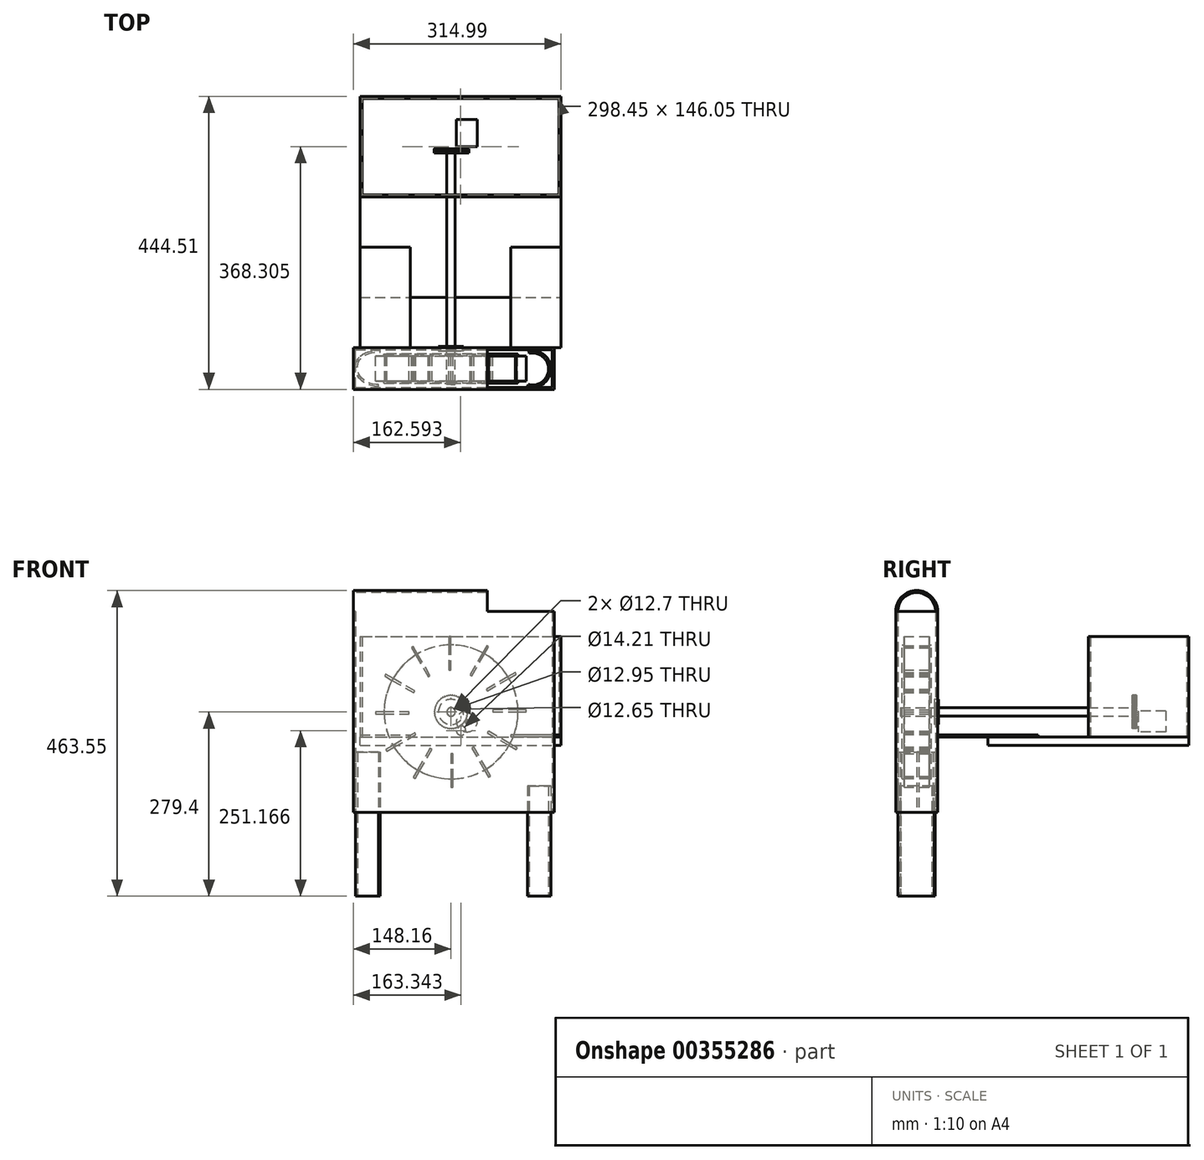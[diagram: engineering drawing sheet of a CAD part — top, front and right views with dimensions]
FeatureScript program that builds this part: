
annotation { "Feature Type Name" : "Feature", "Feature Type Description" : "" }
export const myFeature = defineFeature(function(context is Context, id is Id, definition is map)
    precondition{}
    {
        {
            var Q0;
            Q0=qCreatedBy(makeId("Front.planeOp"),FACE);
            var sketch = newSketch(context, id + "F0", { "sketchPlane" : qUnion([Q0])});
            skCircle(sketch, "E0", {"center": v(0, 0) * mm, "radius": 101.6 * mm});
            skCircle(sketch, "E1", {"center": v(0, 0) * mm, "radius": 6.35 * mm});
            skSolve(sketch);
        }
        {
            var Q0;
            Q0 = qSketchRegion(id + "F0", true);
            extrude(context, id + "F1", {"entities" : qUnion([Q0]), "depth" : 3.17 * mm});
        }
        {
            var Q0;
            Q0=makeQuery(id+"F1.opExtrude","CAP_FACE",FACE,{"disambiguationData":[OSD([sQuery(id+"F0.wireOp",EDGE,"E0"),sQuery(id+"F0.wireOp",EDGE,"E1")])],"isStart":false});
            var sketch = newSketch(context, id + "F2", { "sketchPlane" : qUnion([Q0])});
            skLineSegment(sketch, "E2", {"start": v(0, 101.6) * mm, "end": v(0, 63.5) * mm});
            skLineSegment(sketch, "E3", {"start": v(0, 101.6) * mm, "end": v(0, 114.3) * mm});
            skLineSegment(sketch, "E4", {"start": v(0, 114.3) * mm, "end": v(-3.18, 114.3) * mm});
            skLineSegment(sketch, "E5", {"start": v(-3.17, 114.3) * mm, "end": v(-3.17, 63.5) * mm});
            skLineSegment(sketch, "E6", {"start": v(-3.18, 63.5) * mm, "end": v(0, 63.5) * mm});
            skLineSegment(sketch, "E7.1.0", {"start": v(-59.9, 97.4) * mm, "end": v(-34.5, 53.4) * mm});
            skLineSegment(sketch, "E7.1.1", {"start": v(-50.8, 87.99) * mm, "end": v(-31.75, 55) * mm});
            skLineSegment(sketch, "E7.1.2", {"start": v(-34.5, 53.4) * mm, "end": v(-31.75, 55) * mm});
            skLineSegment(sketch, "E7.1.3", {"start": v(-50.8, 87.99) * mm, "end": v(-57.15, 98.99) * mm});
            skLineSegment(sketch, "E7.1.4", {"start": v(-57.15, 98.99) * mm, "end": v(-59.9, 97.4) * mm});
            skLineSegment(sketch, "E7.2.0", {"start": v(-100.57, 54.4) * mm, "end": v(-56.58, 29) * mm});
            skLineSegment(sketch, "E7.2.1", {"start": v(-87.99, 50.8) * mm, "end": v(-55, 31.75) * mm});
            skLineSegment(sketch, "E7.2.2", {"start": v(-56.58, 29) * mm, "end": v(-55, 31.75) * mm});
            skLineSegment(sketch, "E7.2.3", {"start": v(-87.99, 50.8) * mm, "end": v(-98.99, 57.15) * mm});
            skLineSegment(sketch, "E7.2.4", {"start": v(-98.99, 57.15) * mm, "end": v(-100.57, 54.4) * mm});
            skLineSegment(sketch, "E7.3.0", {"start": v(-114.3, -3.17) * mm, "end": v(-63.5, -3.17) * mm});
            skLineSegment(sketch, "E7.3.1", {"start": v(-101.6, 0) * mm, "end": v(-63.5, 0) * mm});
            skLineSegment(sketch, "E7.3.2", {"start": v(-63.5, -3.17) * mm, "end": v(-63.5, 0) * mm});
            skLineSegment(sketch, "E7.3.3", {"start": v(-101.6, 0) * mm, "end": v(-114.3, 0) * mm});
            skLineSegment(sketch, "E7.3.4", {"start": v(-114.3, 0) * mm, "end": v(-114.3, -3.17) * mm});
            skLineSegment(sketch, "E7.4.0", {"start": v(-97.4, -59.9) * mm, "end": v(-53.4, -34.5) * mm});
            skLineSegment(sketch, "E7.4.1", {"start": v(-87.99, -50.8) * mm, "end": v(-55, -31.75) * mm});
            skLineSegment(sketch, "E7.4.2", {"start": v(-53.4, -34.5) * mm, "end": v(-55, -31.75) * mm});
            skLineSegment(sketch, "E7.4.3", {"start": v(-87.99, -50.8) * mm, "end": v(-98.99, -57.15) * mm});
            skLineSegment(sketch, "E7.4.4", {"start": v(-98.99, -57.15) * mm, "end": v(-97.4, -59.9) * mm});
            skLineSegment(sketch, "E7.5.0", {"start": v(-54.4, -100.57) * mm, "end": v(-29, -56.58) * mm});
            skLineSegment(sketch, "E7.5.1", {"start": v(-50.8, -87.99) * mm, "end": v(-31.75, -55) * mm});
            skLineSegment(sketch, "E7.5.2", {"start": v(-29, -56.58) * mm, "end": v(-31.75, -55) * mm});
            skLineSegment(sketch, "E7.5.3", {"start": v(-50.8, -87.99) * mm, "end": v(-57.15, -98.99) * mm});
            skLineSegment(sketch, "E7.5.4", {"start": v(-57.15, -98.99) * mm, "end": v(-54.4, -100.57) * mm});
            skLineSegment(sketch, "E7.6.0", {"start": v(3.17, -114.3) * mm, "end": v(3.17, -63.5) * mm});
            skLineSegment(sketch, "E7.6.1", {"start": v(0, -101.6) * mm, "end": v(0, -63.5) * mm});
            skLineSegment(sketch, "E7.6.2", {"start": v(3.17, -63.5) * mm, "end": v(0, -63.5) * mm});
            skLineSegment(sketch, "E7.6.3", {"start": v(0, -101.6) * mm, "end": v(0, -114.3) * mm});
            skLineSegment(sketch, "E7.6.4", {"start": v(0, -114.3) * mm, "end": v(3.17, -114.3) * mm});
            skLineSegment(sketch, "E7.7.0", {"start": v(59.9, -97.4) * mm, "end": v(34.5, -53.4) * mm});
            skLineSegment(sketch, "E7.7.1", {"start": v(50.8, -87.99) * mm, "end": v(31.75, -55) * mm});
            skLineSegment(sketch, "E7.7.2", {"start": v(34.5, -53.4) * mm, "end": v(31.75, -55) * mm});
            skLineSegment(sketch, "E7.7.3", {"start": v(50.8, -87.99) * mm, "end": v(57.15, -98.99) * mm});
            skLineSegment(sketch, "E7.7.4", {"start": v(57.15, -98.99) * mm, "end": v(59.9, -97.4) * mm});
            skLineSegment(sketch, "E7.8.0", {"start": v(100.57, -54.4) * mm, "end": v(56.58, -29) * mm});
            skLineSegment(sketch, "E7.8.1", {"start": v(87.99, -50.8) * mm, "end": v(55, -31.75) * mm});
            skLineSegment(sketch, "E7.8.2", {"start": v(56.58, -29) * mm, "end": v(55, -31.75) * mm});
            skLineSegment(sketch, "E7.8.3", {"start": v(87.99, -50.8) * mm, "end": v(98.99, -57.15) * mm});
            skLineSegment(sketch, "E7.8.4", {"start": v(98.99, -57.15) * mm, "end": v(100.57, -54.4) * mm});
            skLineSegment(sketch, "E7.9.0", {"start": v(114.3, 3.17) * mm, "end": v(63.5, 3.17) * mm});
            skLineSegment(sketch, "E7.9.1", {"start": v(101.6, 0) * mm, "end": v(63.5, 0) * mm});
            skLineSegment(sketch, "E7.9.2", {"start": v(63.5, 3.17) * mm, "end": v(63.5, 0) * mm});
            skLineSegment(sketch, "E7.9.3", {"start": v(101.6, 0) * mm, "end": v(114.3, 0) * mm});
            skLineSegment(sketch, "E7.9.4", {"start": v(114.3, 0) * mm, "end": v(114.3, 3.17) * mm});
            skLineSegment(sketch, "E7.10.0", {"start": v(97.4, 59.9) * mm, "end": v(53.4, 34.5) * mm});
            skLineSegment(sketch, "E7.10.1", {"start": v(87.99, 50.8) * mm, "end": v(55, 31.75) * mm});
            skLineSegment(sketch, "E7.10.2", {"start": v(53.4, 34.5) * mm, "end": v(55, 31.75) * mm});
            skLineSegment(sketch, "E7.10.3", {"start": v(87.99, 50.8) * mm, "end": v(98.99, 57.15) * mm});
            skLineSegment(sketch, "E7.10.4", {"start": v(98.99, 57.15) * mm, "end": v(97.4, 59.9) * mm});
            skLineSegment(sketch, "E7.11.0", {"start": v(54.4, 100.57) * mm, "end": v(29, 56.58) * mm});
            skLineSegment(sketch, "E7.11.1", {"start": v(50.8, 87.99) * mm, "end": v(31.75, 55) * mm});
            skLineSegment(sketch, "E7.11.2", {"start": v(29, 56.58) * mm, "end": v(31.75, 55) * mm});
            skLineSegment(sketch, "E7.11.3", {"start": v(50.8, 87.99) * mm, "end": v(57.15, 98.99) * mm});
            skLineSegment(sketch, "E7.11.4", {"start": v(57.15, 98.99) * mm, "end": v(54.4, 100.57) * mm});
            skPoint(sketch, "E7.center", {"position": v(0, 0) * mm});
            skSolve(sketch);
        }
        {
            var Q0;
            Q0 = qSketchRegion(id + "F2", true);
            extrude(context, id + "F3", {"entities" : qUnion([Q0]), "operationType" : NewBodyOperationType.ADD, "depth" : 38.1 * mm});
        }
        {
            var Q0;
            Q0=makeQuery(id+"F3.opExtrude","CAP_FACE",FACE,{"disambiguationData":[OSD([sQuery(id+"F2.wireOp",EDGE,"E7.8.0"),sQuery(id+"F2.wireOp",EDGE,"E7.8.1"),sQuery(id+"F2.wireOp",EDGE,"E7.8.2"),sQuery(id+"F2.wireOp",EDGE,"E7.8.3"),sQuery(id+"F2.wireOp",EDGE,"E7.8.4")])],"isStart":false});
            var sketch = newSketch(context, id + "F4", { "sketchPlane" : qUnion([Q0])});
            skCircle(sketch, "E8", {"center": v(0, 0) * mm, "radius": 101.6 * mm});
            skCircle(sketch, "E9", {"center": v(0, 0) * mm, "radius": 6.35 * mm});
            skCircle(sketch, "E10", {"center": v(0, 0) * mm, "radius": 6.47 * mm});
            skSolve(sketch);
        }
        {
            var Q0;
            Q0 = qSketchRegion(id + "F4", true);
            extrude(context, id + "F5", {"entities" : qUnion([Q0]), "operationType" : NewBodyOperationType.ADD, "depth" : 3.17 * mm});
        }
        {
            var Q0;
            Q0=qCreatedBy(makeId("Front.planeOp"),FACE);
            var sketch = newSketch(context, id + "F6", { "sketchPlane" : qUnion([Q0])});
            skCircle(sketch, "E11", {"center": v(0, 0) * mm, "radius": 6.35 * mm});
            skSolve(sketch);
        }
        {
            var Q0;
            Q0 = qSketchRegion(id + "F6", true);
            extrude(context, id + "F7", {"entities" : qUnion([Q0]), "depth" : 46.74 * mm, "hasSecondDirection" : true, "secondDirectionOppositeDirection" : true, "secondDirectionDepth" : 304.8 * mm});
        }
        {
            var Q0;
            Q0=qCreatedBy(makeId("Top.planeOp"),FACE);
            var sketch = newSketch(context, id + "F8", { "sketchPlane" : qUnion([Q0])});
            skLineSegment(sketch, "E12.bottom", {"start": v(-148.16, 9.53) * mm, "end": v(156.64, 9.53) * mm});
            skLineSegment(sketch, "E12.top", {"start": v(-148.16, -53.97) * mm, "end": v(156.64, -53.97) * mm});
            skLineSegment(sketch, "E12.left", {"start": v(-148.16, 9.53) * mm, "end": v(-148.16, -53.97) * mm});
            skLineSegment(sketch, "E12.right", {"start": v(156.64, 9.52) * mm, "end": v(156.64, -53.97) * mm});
            skLineSegment(sketch, "E13.bottom", {"start": v(-144.98, -50.8) * mm, "end": v(153.47, -50.8) * mm});
            skLineSegment(sketch, "E13.top", {"start": v(-144.98, 6.35) * mm, "end": v(153.47, 6.35) * mm});
            skLineSegment(sketch, "E13.left", {"start": v(-144.98, -50.8) * mm, "end": v(-144.98, 6.35) * mm});
            skLineSegment(sketch, "E13.right", {"start": v(153.47, -50.8) * mm, "end": v(153.47, 6.35) * mm});
            skSolve(sketch);
        }
        {
            var Q0;
            Q0 = qSketchRegion(id + "F8", true);
            extrude(context, id + "F9", {"entities" : qUnion([Q0]), "depth" : 152.4 * mm, "hasSecondDirection" : true, "secondDirectionOppositeDirection" : true, "secondDirectionDepth" : 152.4 * mm});
        }
        {
            var Q0;
            Q0=makeQuery(id+"F9.opExtrude","SWEPT_FACE",FACE,{"disambiguationData":[OSD([sQuery(id+"F8.wireOp",EDGE,"E12.bottom")])]});
            var sketch = newSketch(context, id + "F10", { "sketchPlane" : qUnion([Q0])});
            skCircle(sketch, "E14", {"center": v(0, 0) * mm, "radius": 6.35 * mm});
            skCircle(sketch, "E15", {"center": v(0, 0) * mm, "radius": 19.05 * mm});
            skSolve(sketch);
        }
        {
            var Q0;
            Q0=makeQuery(id+"F10.imprint","IMPRINT",FACE,{"disambiguationData":[TD([[makeQuery(id+"F10.imprint","IMPRINT",EDGE,{"derivedFrom":sQuery(id+"F10.wireOp",EDGE,"E14")}),1.0]])]});
            extrude(context, id + "F11", {"entities" : qUnion([Q0]), "operationType" : NewBodyOperationType.REMOVE, "oppositeDirection" : true, "depth" : 3.17 * mm});
        }
        {
            var Q0;
            Q0=makeQuery(id+"F9.opExtrude","SWEPT_FACE",FACE,{"disambiguationData":[OSD([sQuery(id+"F8.wireOp",EDGE,"E12.bottom")])]});
            var sketch = newSketch(context, id + "F12", { "sketchPlane" : qUnion([Q0])});
            skCircle(sketch, "E16", {"center": v(0, 0) * mm, "radius": 19.05 * mm});
            skCircle(sketch, "E17", {"center": v(0, 0) * mm, "radius": 6.33 * mm});
            skSolve(sketch);
        }
        {
            var Q0;
            Q0 = qSketchRegion(id + "F12", true);
            extrude(context, id + "F13", {"entities" : qUnion([Q0]), "depth" : 1.63 * mm, "hasSecondDirection" : true, "secondDirectionOppositeDirection" : true, "secondDirectionDepth" : 5.23 * mm});
        }
        {
            var Q0;
            Q0=qCreatedBy(makeId("Top.planeOp"),FACE);
            var sketch = newSketch(context, id + "F14", { "sketchPlane" : qUnion([Q0])});
            skLineSegment(sketch, "E18.bottom", {"start": v(-137.97, 85.72) * mm, "end": v(166.83, 85.72) * mm});
            skLineSegment(sketch, "E18.top", {"start": v(-137.97, 390.53) * mm, "end": v(166.83, 390.53) * mm});
            skLineSegment(sketch, "E18.left", {"start": v(-137.97, 85.72) * mm, "end": v(-137.97, 390.53) * mm});
            skLineSegment(sketch, "E18.right", {"start": v(166.83, 85.73) * mm, "end": v(166.83, 390.53) * mm});
            skSolve(sketch);
        }
        {
            var Q0;
            Q0=makeQuery(id+"F14.imprint","IMPRINT",FACE,{"disambiguationData":[TD([[makeQuery(id+"F14.imprint","IMPRINT",EDGE,{"derivedFrom":sQuery(id+"F14.wireOp",EDGE,"E18.bottom")}),1.0]])]});
            extrude(context, id + "F15", {"entities" : qUnion([Q0]), "oppositeDirection" : true, "depth" : 50.8 * mm, "hasSecondDirection" : true, "secondDirectionOppositeDirection" : true, "secondDirectionDepth" : 38.1 * mm});
        }
        {
            var Q0;
            Q0=makeQuery(id+"F15.opExtrude","CAP_FACE",FACE,{"disambiguationData":[OSD([sQuery(id+"F14.wireOp",EDGE,"E18.bottom"),sQuery(id+"F14.wireOp",EDGE,"E18.top"),sQuery(id+"F14.wireOp",EDGE,"E18.left"),sQuery(id+"F14.wireOp",EDGE,"E18.right")])],"isStart":true});
            var sketch = newSketch(context, id + "F16", { "sketchPlane" : qUnion([Q0])});
            skLineSegment(sketch, "E19.bottom", {"start": v(-137.97, 390.53) * mm, "end": v(166.83, 390.53) * mm});
            skLineSegment(sketch, "E19.top", {"start": v(-137.97, 238.13) * mm, "end": v(166.83, 238.13) * mm});
            skLineSegment(sketch, "E19.left", {"start": v(-137.97, 390.53) * mm, "end": v(-137.97, 238.13) * mm});
            skLineSegment(sketch, "E19.right", {"start": v(166.83, 390.53) * mm, "end": v(166.83, 238.13) * mm});
            skLineSegment(sketch, "E20.0", {"start": v(-134.8, 387.35) * mm, "end": v(-134.8, 241.3) * mm});
            skLineSegment(sketch, "E20.1", {"start": v(-134.8, 387.35) * mm, "end": v(163.66, 387.35) * mm});
            skLineSegment(sketch, "E20.2", {"start": v(163.66, 387.35) * mm, "end": v(163.66, 241.3) * mm});
            skLineSegment(sketch, "E20.3", {"start": v(-134.8, 241.3) * mm, "end": v(163.66, 241.3) * mm});
            skSolve(sketch);
        }
        {
            var Q0;
            Q0 = qSketchRegion(id + "F16", true);
            extrude(context, id + "F17", {"entities" : qUnion([Q0]), "depth" : 152.4 * mm});
        }
        {
            var Q0;
            Q0=makeQuery(id+"F7.opExtrude","CAP_FACE",FACE,{"disambiguationData":[OSD([sQuery(id+"F6.wireOp",EDGE,"E11")])],"isStart":true});
            var sketch = newSketch(context, id + "F18", { "sketchPlane" : qUnion([Q0])});
            skCircle(sketch, "E21", {"center": v(0, 0) * mm, "radius": 25.4 * mm});
            skLineSegment(sketch, "E22", {"start": v(0, 25.4) * mm, "end": v(0, 24.9) * mm});
            skLineSegment(sketch, "E23", {"start": v(1.6, 25.35) * mm, "end": v(1.56, 24.84) * mm});
            skLineSegment(sketch, "E24", {"start": v(0, 24.9) * mm, "end": v(0.38, 25.4) * mm});
            skLineSegment(sketch, "E25", {"start": v(0.38, 25.4) * mm, "end": v(1.21, 25.37) * mm});
            skLineSegment(sketch, "E26", {"start": v(1.21, 25.37) * mm, "end": v(1.56, 24.84) * mm});
            skLineSegment(sketch, "E27.1.0", {"start": v(-1.98, 25.32) * mm, "end": v(-1.56, 24.84) * mm});
            skLineSegment(sketch, "E27.1.1", {"start": v(-2.8, 25.25) * mm, "end": v(-1.98, 25.32) * mm});
            skLineSegment(sketch, "E27.1.2", {"start": v(-3.12, 24.7) * mm, "end": v(-2.8, 25.25) * mm});
            skLineSegment(sketch, "E27.2.0", {"start": v(-5.14, 24.88) * mm, "end": v(-4.66, 24.45) * mm});
            skLineSegment(sketch, "E27.2.1", {"start": v(-5.94, 24.7) * mm, "end": v(-5.14, 24.88) * mm});
            skLineSegment(sketch, "E27.2.2", {"start": v(-6.2, 24.1) * mm, "end": v(-5.94, 24.7) * mm});
            skLineSegment(sketch, "E27.3.0", {"start": v(-8.21, 24.04) * mm, "end": v(-7.7, 23.67) * mm});
            skLineSegment(sketch, "E27.3.1", {"start": v(-9, 23.76) * mm, "end": v(-8.21, 24.04) * mm});
            skLineSegment(sketch, "E27.3.2", {"start": v(-9.16, 23.14) * mm, "end": v(-9, 23.76) * mm});
            skLineSegment(sketch, "E27.4.0", {"start": v(-11.16, 22.82) * mm, "end": v(-10.6, 22.52) * mm});
            skLineSegment(sketch, "E27.4.1", {"start": v(-11.9, 22.44) * mm, "end": v(-11.16, 22.82) * mm});
            skLineSegment(sketch, "E27.4.2", {"start": v(-12, 21.81) * mm, "end": v(-11.9, 22.44) * mm});
            skLineSegment(sketch, "E27.5.0", {"start": v(-13.93, 21.24) * mm, "end": v(-13.34, 21.02) * mm});
            skLineSegment(sketch, "E27.5.1", {"start": v(-14.62, 20.77) * mm, "end": v(-13.93, 21.24) * mm});
            skLineSegment(sketch, "E27.5.2", {"start": v(-14.63, 20.14) * mm, "end": v(-14.62, 20.77) * mm});
            skLineSegment(sketch, "E27.6.0", {"start": v(-16.49, 19.32) * mm, "end": v(-15.87, 19.18) * mm});
            skLineSegment(sketch, "E27.6.1", {"start": v(-17.1, 18.78) * mm, "end": v(-16.49, 19.32) * mm});
            skLineSegment(sketch, "E27.6.2", {"start": v(-17.04, 18.15) * mm, "end": v(-17.1, 18.78) * mm});
            skLineSegment(sketch, "E27.7.0", {"start": v(-18.78, 17.1) * mm, "end": v(-18.15, 17.04) * mm});
            skLineSegment(sketch, "E27.7.1", {"start": v(-19.32, 16.49) * mm, "end": v(-18.78, 17.1) * mm});
            skLineSegment(sketch, "E27.7.2", {"start": v(-19.18, 15.87) * mm, "end": v(-19.32, 16.49) * mm});
            skLineSegment(sketch, "E27.8.0", {"start": v(-20.77, 14.62) * mm, "end": v(-20.14, 14.63) * mm});
            skLineSegment(sketch, "E27.8.1", {"start": v(-21.24, 13.93) * mm, "end": v(-20.77, 14.62) * mm});
            skLineSegment(sketch, "E27.8.2", {"start": v(-21.02, 13.34) * mm, "end": v(-21.24, 13.93) * mm});
            skLineSegment(sketch, "E27.9.0", {"start": v(-22.44, 11.9) * mm, "end": v(-21.81, 12) * mm});
            skLineSegment(sketch, "E27.9.1", {"start": v(-22.82, 11.16) * mm, "end": v(-22.44, 11.9) * mm});
            skLineSegment(sketch, "E27.9.2", {"start": v(-22.52, 10.6) * mm, "end": v(-22.82, 11.16) * mm});
            skLineSegment(sketch, "E27.10.0", {"start": v(-23.76, 9) * mm, "end": v(-23.14, 9.16) * mm});
            skLineSegment(sketch, "E27.10.1", {"start": v(-24.04, 8.21) * mm, "end": v(-23.76, 9) * mm});
            skLineSegment(sketch, "E27.10.2", {"start": v(-23.67, 7.7) * mm, "end": v(-24.04, 8.21) * mm});
            skLineSegment(sketch, "E27.11.0", {"start": v(-24.7, 5.94) * mm, "end": v(-24.1, 6.2) * mm});
            skLineSegment(sketch, "E27.11.1", {"start": v(-24.88, 5.14) * mm, "end": v(-24.7, 5.94) * mm});
            skLineSegment(sketch, "E27.11.2", {"start": v(-24.45, 4.66) * mm, "end": v(-24.88, 5.14) * mm});
            skLineSegment(sketch, "E27.12.0", {"start": v(-25.25, 2.8) * mm, "end": v(-24.7, 3.12) * mm});
            skLineSegment(sketch, "E27.12.1", {"start": v(-25.32, 1.98) * mm, "end": v(-25.25, 2.8) * mm});
            skLineSegment(sketch, "E27.12.2", {"start": v(-24.84, 1.56) * mm, "end": v(-25.32, 1.98) * mm});
            skLineSegment(sketch, "E27.13.0", {"start": v(-25.4, -0.38) * mm, "end": v(-24.9, 0) * mm});
            skLineSegment(sketch, "E27.13.1", {"start": v(-25.37, -1.21) * mm, "end": v(-25.4, -0.38) * mm});
            skLineSegment(sketch, "E27.13.2", {"start": v(-24.84, -1.56) * mm, "end": v(-25.37, -1.21) * mm});
            skLineSegment(sketch, "E27.14.0", {"start": v(-25.15, -3.56) * mm, "end": v(-24.7, -3.12) * mm});
            skLineSegment(sketch, "E27.14.1", {"start": v(-25.02, -4.38) * mm, "end": v(-25.15, -3.56) * mm});
            skLineSegment(sketch, "E27.14.2", {"start": v(-24.45, -4.66) * mm, "end": v(-25.02, -4.38) * mm});
            skLineSegment(sketch, "E27.15.0", {"start": v(-24.5, -6.69) * mm, "end": v(-24.1, -6.2) * mm});
            skLineSegment(sketch, "E27.15.1", {"start": v(-24.27, -7.48) * mm, "end": v(-24.5, -6.69) * mm});
            skLineSegment(sketch, "E27.15.2", {"start": v(-23.67, -7.7) * mm, "end": v(-24.27, -7.48) * mm});
            skLineSegment(sketch, "E27.16.0", {"start": v(-23.47, -9.7) * mm, "end": v(-23.14, -9.16) * mm});
            skLineSegment(sketch, "E27.16.1", {"start": v(-23.14, -10.47) * mm, "end": v(-23.47, -9.7) * mm});
            skLineSegment(sketch, "E27.16.2", {"start": v(-22.52, -10.6) * mm, "end": v(-23.14, -10.47) * mm});
            skLineSegment(sketch, "E27.17.0", {"start": v(-22.07, -12.57) * mm, "end": v(-21.81, -12) * mm});
            skLineSegment(sketch, "E27.17.1", {"start": v(-21.65, -13.28) * mm, "end": v(-22.07, -12.57) * mm});
            skLineSegment(sketch, "E27.17.2", {"start": v(-21.02, -13.34) * mm, "end": v(-21.65, -13.28) * mm});
            skLineSegment(sketch, "E27.18.0", {"start": v(-20.32, -15.24) * mm, "end": v(-20.14, -14.63) * mm});
            skLineSegment(sketch, "E27.18.1", {"start": v(-19.81, -15.9) * mm, "end": v(-20.32, -15.24) * mm});
            skLineSegment(sketch, "E27.18.2", {"start": v(-19.18, -15.87) * mm, "end": v(-19.81, -15.9) * mm});
            skLineSegment(sketch, "E27.19.0", {"start": v(-18.25, -17.67) * mm, "end": v(-18.15, -17.04) * mm});
            skLineSegment(sketch, "E27.19.1", {"start": v(-17.67, -18.25) * mm, "end": v(-18.25, -17.67) * mm});
            skLineSegment(sketch, "E27.19.2", {"start": v(-17.04, -18.15) * mm, "end": v(-17.67, -18.25) * mm});
            skLineSegment(sketch, "E27.20.0", {"start": v(-15.9, -19.81) * mm, "end": v(-15.87, -19.18) * mm});
            skLineSegment(sketch, "E27.20.1", {"start": v(-15.24, -20.32) * mm, "end": v(-15.9, -19.81) * mm});
            skLineSegment(sketch, "E27.20.2", {"start": v(-14.63, -20.14) * mm, "end": v(-15.24, -20.32) * mm});
            skLineSegment(sketch, "E27.21.0", {"start": v(-13.28, -21.65) * mm, "end": v(-13.34, -21.02) * mm});
            skLineSegment(sketch, "E27.21.1", {"start": v(-12.57, -22.07) * mm, "end": v(-13.28, -21.65) * mm});
            skLineSegment(sketch, "E27.21.2", {"start": v(-12, -21.81) * mm, "end": v(-12.57, -22.07) * mm});
            skLineSegment(sketch, "E27.22.0", {"start": v(-10.47, -23.14) * mm, "end": v(-10.6, -22.52) * mm});
            skLineSegment(sketch, "E27.22.1", {"start": v(-9.7, -23.47) * mm, "end": v(-10.47, -23.14) * mm});
            skLineSegment(sketch, "E27.22.2", {"start": v(-9.16, -23.14) * mm, "end": v(-9.7, -23.47) * mm});
            skLineSegment(sketch, "E27.23.0", {"start": v(-7.48, -24.27) * mm, "end": v(-7.7, -23.67) * mm});
            skLineSegment(sketch, "E27.23.1", {"start": v(-6.69, -24.5) * mm, "end": v(-7.48, -24.27) * mm});
            skLineSegment(sketch, "E27.23.2", {"start": v(-6.2, -24.1) * mm, "end": v(-6.69, -24.5) * mm});
            skLineSegment(sketch, "E27.24.0", {"start": v(-4.38, -25.02) * mm, "end": v(-4.66, -24.45) * mm});
            skLineSegment(sketch, "E27.24.1", {"start": v(-3.56, -25.15) * mm, "end": v(-4.38, -25.02) * mm});
            skLineSegment(sketch, "E27.24.2", {"start": v(-3.12, -24.7) * mm, "end": v(-3.56, -25.15) * mm});
            skLineSegment(sketch, "E27.25.0", {"start": v(-1.21, -25.37) * mm, "end": v(-1.56, -24.84) * mm});
            skLineSegment(sketch, "E27.25.1", {"start": v(-0.38, -25.4) * mm, "end": v(-1.21, -25.37) * mm});
            skLineSegment(sketch, "E27.25.2", {"start": v(0, -24.9) * mm, "end": v(-0.38, -25.4) * mm});
            skLineSegment(sketch, "E27.26.0", {"start": v(1.98, -25.32) * mm, "end": v(1.56, -24.84) * mm});
            skLineSegment(sketch, "E27.26.1", {"start": v(2.8, -25.25) * mm, "end": v(1.98, -25.32) * mm});
            skLineSegment(sketch, "E27.26.2", {"start": v(3.12, -24.7) * mm, "end": v(2.8, -25.25) * mm});
            skLineSegment(sketch, "E27.27.0", {"start": v(5.14, -24.88) * mm, "end": v(4.66, -24.45) * mm});
            skLineSegment(sketch, "E27.27.1", {"start": v(5.94, -24.7) * mm, "end": v(5.14, -24.88) * mm});
            skLineSegment(sketch, "E27.27.2", {"start": v(6.2, -24.1) * mm, "end": v(5.94, -24.7) * mm});
            skLineSegment(sketch, "E27.28.0", {"start": v(8.21, -24.04) * mm, "end": v(7.7, -23.67) * mm});
            skLineSegment(sketch, "E27.28.1", {"start": v(9, -23.76) * mm, "end": v(8.21, -24.04) * mm});
            skLineSegment(sketch, "E27.28.2", {"start": v(9.16, -23.14) * mm, "end": v(9, -23.76) * mm});
            skLineSegment(sketch, "E27.29.0", {"start": v(11.16, -22.82) * mm, "end": v(10.6, -22.52) * mm});
            skLineSegment(sketch, "E27.29.1", {"start": v(11.9, -22.44) * mm, "end": v(11.16, -22.82) * mm});
            skLineSegment(sketch, "E27.29.2", {"start": v(12, -21.81) * mm, "end": v(11.9, -22.44) * mm});
            skLineSegment(sketch, "E27.30.0", {"start": v(13.93, -21.24) * mm, "end": v(13.34, -21.02) * mm});
            skLineSegment(sketch, "E27.30.1", {"start": v(14.62, -20.77) * mm, "end": v(13.93, -21.24) * mm});
            skLineSegment(sketch, "E27.30.2", {"start": v(14.63, -20.14) * mm, "end": v(14.62, -20.77) * mm});
            skLineSegment(sketch, "E27.31.0", {"start": v(16.49, -19.32) * mm, "end": v(15.87, -19.18) * mm});
            skLineSegment(sketch, "E27.31.1", {"start": v(17.1, -18.78) * mm, "end": v(16.49, -19.32) * mm});
            skLineSegment(sketch, "E27.31.2", {"start": v(17.04, -18.15) * mm, "end": v(17.1, -18.78) * mm});
            skLineSegment(sketch, "E27.32.0", {"start": v(18.78, -17.1) * mm, "end": v(18.15, -17.04) * mm});
            skLineSegment(sketch, "E27.32.1", {"start": v(19.32, -16.49) * mm, "end": v(18.78, -17.1) * mm});
            skLineSegment(sketch, "E27.32.2", {"start": v(19.18, -15.87) * mm, "end": v(19.32, -16.49) * mm});
            skLineSegment(sketch, "E27.33.0", {"start": v(20.77, -14.62) * mm, "end": v(20.14, -14.63) * mm});
            skLineSegment(sketch, "E27.33.1", {"start": v(21.24, -13.93) * mm, "end": v(20.77, -14.62) * mm});
            skLineSegment(sketch, "E27.33.2", {"start": v(21.02, -13.34) * mm, "end": v(21.24, -13.93) * mm});
            skLineSegment(sketch, "E27.34.0", {"start": v(22.44, -11.9) * mm, "end": v(21.81, -12) * mm});
            skLineSegment(sketch, "E27.34.1", {"start": v(22.82, -11.16) * mm, "end": v(22.44, -11.9) * mm});
            skLineSegment(sketch, "E27.34.2", {"start": v(22.52, -10.6) * mm, "end": v(22.82, -11.16) * mm});
            skLineSegment(sketch, "E27.35.0", {"start": v(23.76, -9) * mm, "end": v(23.14, -9.16) * mm});
            skLineSegment(sketch, "E27.35.1", {"start": v(24.04, -8.21) * mm, "end": v(23.76, -9) * mm});
            skLineSegment(sketch, "E27.35.2", {"start": v(23.67, -7.7) * mm, "end": v(24.04, -8.21) * mm});
            skLineSegment(sketch, "E27.36.0", {"start": v(24.7, -5.94) * mm, "end": v(24.1, -6.2) * mm});
            skLineSegment(sketch, "E27.36.1", {"start": v(24.88, -5.14) * mm, "end": v(24.7, -5.94) * mm});
            skLineSegment(sketch, "E27.36.2", {"start": v(24.45, -4.66) * mm, "end": v(24.88, -5.14) * mm});
            skLineSegment(sketch, "E27.37.0", {"start": v(25.25, -2.8) * mm, "end": v(24.7, -3.12) * mm});
            skLineSegment(sketch, "E27.37.1", {"start": v(25.32, -1.98) * mm, "end": v(25.25, -2.8) * mm});
            skLineSegment(sketch, "E27.37.2", {"start": v(24.84, -1.56) * mm, "end": v(25.32, -1.98) * mm});
            skLineSegment(sketch, "E27.38.0", {"start": v(25.4, 0.38) * mm, "end": v(24.9, 0) * mm});
            skLineSegment(sketch, "E27.38.1", {"start": v(25.37, 1.21) * mm, "end": v(25.4, 0.38) * mm});
            skLineSegment(sketch, "E27.38.2", {"start": v(24.84, 1.56) * mm, "end": v(25.37, 1.21) * mm});
            skLineSegment(sketch, "E27.39.0", {"start": v(25.15, 3.56) * mm, "end": v(24.7, 3.12) * mm});
            skLineSegment(sketch, "E27.39.1", {"start": v(25.02, 4.38) * mm, "end": v(25.15, 3.56) * mm});
            skLineSegment(sketch, "E27.39.2", {"start": v(24.45, 4.66) * mm, "end": v(25.02, 4.38) * mm});
            skLineSegment(sketch, "E27.40.0", {"start": v(24.5, 6.69) * mm, "end": v(24.1, 6.2) * mm});
            skLineSegment(sketch, "E27.40.1", {"start": v(24.27, 7.48) * mm, "end": v(24.5, 6.69) * mm});
            skLineSegment(sketch, "E27.40.2", {"start": v(23.67, 7.7) * mm, "end": v(24.27, 7.48) * mm});
            skLineSegment(sketch, "E27.41.0", {"start": v(23.47, 9.7) * mm, "end": v(23.14, 9.16) * mm});
            skLineSegment(sketch, "E27.41.1", {"start": v(23.14, 10.47) * mm, "end": v(23.47, 9.7) * mm});
            skLineSegment(sketch, "E27.41.2", {"start": v(22.52, 10.6) * mm, "end": v(23.14, 10.47) * mm});
            skLineSegment(sketch, "E27.42.0", {"start": v(22.07, 12.57) * mm, "end": v(21.81, 12) * mm});
            skLineSegment(sketch, "E27.42.1", {"start": v(21.65, 13.28) * mm, "end": v(22.07, 12.57) * mm});
            skLineSegment(sketch, "E27.42.2", {"start": v(21.02, 13.34) * mm, "end": v(21.65, 13.28) * mm});
            skLineSegment(sketch, "E27.43.0", {"start": v(20.32, 15.24) * mm, "end": v(20.14, 14.63) * mm});
            skLineSegment(sketch, "E27.43.1", {"start": v(19.81, 15.9) * mm, "end": v(20.32, 15.24) * mm});
            skLineSegment(sketch, "E27.43.2", {"start": v(19.18, 15.87) * mm, "end": v(19.81, 15.9) * mm});
            skLineSegment(sketch, "E27.44.0", {"start": v(18.25, 17.67) * mm, "end": v(18.15, 17.04) * mm});
            skLineSegment(sketch, "E27.44.1", {"start": v(17.67, 18.25) * mm, "end": v(18.25, 17.67) * mm});
            skLineSegment(sketch, "E27.44.2", {"start": v(17.04, 18.15) * mm, "end": v(17.67, 18.25) * mm});
            skLineSegment(sketch, "E27.45.0", {"start": v(15.9, 19.81) * mm, "end": v(15.87, 19.18) * mm});
            skLineSegment(sketch, "E27.45.1", {"start": v(15.24, 20.32) * mm, "end": v(15.9, 19.81) * mm});
            skLineSegment(sketch, "E27.45.2", {"start": v(14.63, 20.14) * mm, "end": v(15.24, 20.32) * mm});
            skLineSegment(sketch, "E27.46.0", {"start": v(13.28, 21.65) * mm, "end": v(13.34, 21.02) * mm});
            skLineSegment(sketch, "E27.46.1", {"start": v(12.57, 22.07) * mm, "end": v(13.28, 21.65) * mm});
            skLineSegment(sketch, "E27.46.2", {"start": v(12, 21.81) * mm, "end": v(12.57, 22.07) * mm});
            skLineSegment(sketch, "E27.47.0", {"start": v(10.47, 23.14) * mm, "end": v(10.6, 22.52) * mm});
            skLineSegment(sketch, "E27.47.1", {"start": v(9.7, 23.47) * mm, "end": v(10.47, 23.14) * mm});
            skLineSegment(sketch, "E27.47.2", {"start": v(9.16, 23.14) * mm, "end": v(9.7, 23.47) * mm});
            skLineSegment(sketch, "E27.48.0", {"start": v(7.48, 24.27) * mm, "end": v(7.7, 23.67) * mm});
            skLineSegment(sketch, "E27.48.1", {"start": v(6.69, 24.5) * mm, "end": v(7.48, 24.27) * mm});
            skLineSegment(sketch, "E27.48.2", {"start": v(6.2, 24.1) * mm, "end": v(6.69, 24.5) * mm});
            skLineSegment(sketch, "E27.49.0", {"start": v(4.38, 25.02) * mm, "end": v(4.66, 24.45) * mm});
            skLineSegment(sketch, "E27.49.1", {"start": v(3.56, 25.15) * mm, "end": v(4.38, 25.02) * mm});
            skLineSegment(sketch, "E27.49.2", {"start": v(3.12, 24.7) * mm, "end": v(3.56, 25.15) * mm});
            skLineSegment(sketch, "E28", {"start": v(1.56, 24.84) * mm, "end": v(3.12, 24.7) * mm});
            skLineSegment(sketch, "E29.1.0", {"start": v(-1.56, 24.84) * mm, "end": v(0, 24.9) * mm});
            skLineSegment(sketch, "E29.2.0", {"start": v(-4.66, 24.45) * mm, "end": v(-3.12, 24.7) * mm});
            skLineSegment(sketch, "E29.3.0", {"start": v(-7.7, 23.67) * mm, "end": v(-6.2, 24.1) * mm});
            skLineSegment(sketch, "E29.4.0", {"start": v(-10.6, 22.52) * mm, "end": v(-9.16, 23.14) * mm});
            skLineSegment(sketch, "E29.5.0", {"start": v(-13.34, 21.02) * mm, "end": v(-12, 21.81) * mm});
            skLineSegment(sketch, "E29.6.0", {"start": v(-15.87, 19.18) * mm, "end": v(-14.63, 20.14) * mm});
            skLineSegment(sketch, "E29.7.0", {"start": v(-18.15, 17.04) * mm, "end": v(-17.04, 18.15) * mm});
            skLineSegment(sketch, "E29.8.0", {"start": v(-20.14, 14.63) * mm, "end": v(-19.18, 15.87) * mm});
            skLineSegment(sketch, "E29.9.0", {"start": v(-21.81, 12) * mm, "end": v(-21.02, 13.34) * mm});
            skLineSegment(sketch, "E29.10.0", {"start": v(-23.14, 9.16) * mm, "end": v(-22.52, 10.6) * mm});
            skLineSegment(sketch, "E29.11.0", {"start": v(-24.1, 6.2) * mm, "end": v(-23.67, 7.7) * mm});
            skLineSegment(sketch, "E29.12.0", {"start": v(-24.7, 3.12) * mm, "end": v(-24.45, 4.66) * mm});
            skLineSegment(sketch, "E29.13.0", {"start": v(-24.9, 0) * mm, "end": v(-24.84, 1.56) * mm});
            skLineSegment(sketch, "E29.14.0", {"start": v(-24.7, -3.12) * mm, "end": v(-24.84, -1.56) * mm});
            skLineSegment(sketch, "E29.15.0", {"start": v(-24.1, -6.2) * mm, "end": v(-24.45, -4.66) * mm});
            skLineSegment(sketch, "E29.16.0", {"start": v(-23.14, -9.16) * mm, "end": v(-23.67, -7.7) * mm});
            skLineSegment(sketch, "E29.17.0", {"start": v(-21.81, -12) * mm, "end": v(-22.52, -10.6) * mm});
            skLineSegment(sketch, "E29.18.0", {"start": v(-20.14, -14.63) * mm, "end": v(-21.02, -13.34) * mm});
            skLineSegment(sketch, "E29.19.0", {"start": v(-18.15, -17.04) * mm, "end": v(-19.18, -15.87) * mm});
            skLineSegment(sketch, "E29.20.0", {"start": v(-15.87, -19.18) * mm, "end": v(-17.04, -18.15) * mm});
            skLineSegment(sketch, "E29.21.0", {"start": v(-13.34, -21.02) * mm, "end": v(-14.63, -20.14) * mm});
            skLineSegment(sketch, "E29.22.0", {"start": v(-10.6, -22.52) * mm, "end": v(-12, -21.81) * mm});
            skLineSegment(sketch, "E29.23.0", {"start": v(-7.7, -23.67) * mm, "end": v(-9.16, -23.14) * mm});
            skLineSegment(sketch, "E29.24.0", {"start": v(-4.66, -24.45) * mm, "end": v(-6.2, -24.1) * mm});
            skLineSegment(sketch, "E29.25.0", {"start": v(-1.56, -24.84) * mm, "end": v(-3.12, -24.7) * mm});
            skLineSegment(sketch, "E29.26.0", {"start": v(1.56, -24.84) * mm, "end": v(0, -24.9) * mm});
            skLineSegment(sketch, "E29.27.0", {"start": v(4.66, -24.45) * mm, "end": v(3.12, -24.7) * mm});
            skLineSegment(sketch, "E29.28.0", {"start": v(7.7, -23.67) * mm, "end": v(6.2, -24.1) * mm});
            skLineSegment(sketch, "E29.29.0", {"start": v(10.6, -22.52) * mm, "end": v(9.16, -23.14) * mm});
            skLineSegment(sketch, "E29.30.0", {"start": v(13.34, -21.02) * mm, "end": v(12, -21.81) * mm});
            skLineSegment(sketch, "E29.31.0", {"start": v(15.87, -19.18) * mm, "end": v(14.63, -20.14) * mm});
            skLineSegment(sketch, "E29.32.0", {"start": v(18.15, -17.04) * mm, "end": v(17.04, -18.15) * mm});
            skLineSegment(sketch, "E29.33.0", {"start": v(20.14, -14.63) * mm, "end": v(19.18, -15.87) * mm});
            skLineSegment(sketch, "E29.34.0", {"start": v(21.81, -12) * mm, "end": v(21.02, -13.34) * mm});
            skLineSegment(sketch, "E29.35.0", {"start": v(23.14, -9.16) * mm, "end": v(22.52, -10.6) * mm});
            skLineSegment(sketch, "E29.36.0", {"start": v(24.1, -6.2) * mm, "end": v(23.67, -7.7) * mm});
            skLineSegment(sketch, "E29.37.0", {"start": v(24.7, -3.12) * mm, "end": v(24.45, -4.66) * mm});
            skLineSegment(sketch, "E29.38.0", {"start": v(24.9, 0) * mm, "end": v(24.84, -1.56) * mm});
            skLineSegment(sketch, "E29.39.0", {"start": v(24.7, 3.12) * mm, "end": v(24.84, 1.56) * mm});
            skLineSegment(sketch, "E29.40.0", {"start": v(24.1, 6.2) * mm, "end": v(24.45, 4.66) * mm});
            skLineSegment(sketch, "E29.41.0", {"start": v(23.14, 9.16) * mm, "end": v(23.67, 7.7) * mm});
            skLineSegment(sketch, "E29.42.0", {"start": v(21.81, 12) * mm, "end": v(22.52, 10.6) * mm});
            skLineSegment(sketch, "E29.43.0", {"start": v(20.14, 14.63) * mm, "end": v(21.02, 13.34) * mm});
            skLineSegment(sketch, "E29.44.0", {"start": v(18.15, 17.04) * mm, "end": v(19.18, 15.87) * mm});
            skLineSegment(sketch, "E29.45.0", {"start": v(15.87, 19.18) * mm, "end": v(17.04, 18.15) * mm});
            skLineSegment(sketch, "E29.46.0", {"start": v(13.34, 21.02) * mm, "end": v(14.63, 20.14) * mm});
            skLineSegment(sketch, "E29.47.0", {"start": v(10.6, 22.52) * mm, "end": v(12, 21.81) * mm});
            skLineSegment(sketch, "E29.48.0", {"start": v(7.7, 23.67) * mm, "end": v(9.16, 23.14) * mm});
            skLineSegment(sketch, "E29.49.0", {"start": v(4.66, 24.45) * mm, "end": v(6.2, 24.1) * mm});
            skSolve(sketch);
        }
        {
            var Q0;
            {var subQ0=sQuery(id+"F18.wireOp",EDGE,"E27.38.1");Q0=makeQuery(id+"F18.imprint","IMPRINT",FACE,{"disambiguationData":[TD([[makeQuery(id+"F18.imprint","IMPRINT",EDGE,{"derivedFrom":subQ0}),1.0]])]});}
            var Q1;
            {var subQ0=sQuery(id+"F18.wireOp",EDGE,"E27.39.1");Q1=makeQuery(id+"F18.imprint","IMPRINT",FACE,{"disambiguationData":[TD([[makeQuery(id+"F18.imprint","IMPRINT",EDGE,{"derivedFrom":subQ0}),1.0]])]});}
            var Q2;
            {var subQ0=sQuery(id+"F18.wireOp",EDGE,"E27.40.1");Q2=makeQuery(id+"F18.imprint","IMPRINT",FACE,{"disambiguationData":[TD([[makeQuery(id+"F18.imprint","IMPRINT",EDGE,{"derivedFrom":subQ0}),1.0]])]});}
            var Q3;
            {var subQ0=sQuery(id+"F18.wireOp",EDGE,"E27.41.1");Q3=makeQuery(id+"F18.imprint","IMPRINT",FACE,{"disambiguationData":[TD([[makeQuery(id+"F18.imprint","IMPRINT",EDGE,{"derivedFrom":subQ0}),1.0]])]});}
            var Q4;
            {var subQ0=sQuery(id+"F18.wireOp",EDGE,"E27.42.1");Q4=makeQuery(id+"F18.imprint","IMPRINT",FACE,{"disambiguationData":[TD([[makeQuery(id+"F18.imprint","IMPRINT",EDGE,{"derivedFrom":subQ0}),1.0]])]});}
            var Q5;
            {var subQ0=sQuery(id+"F18.wireOp",EDGE,"E27.43.1");Q5=makeQuery(id+"F18.imprint","IMPRINT",FACE,{"disambiguationData":[TD([[makeQuery(id+"F18.imprint","IMPRINT",EDGE,{"derivedFrom":subQ0}),1.0]])]});}
            var Q6;
            {var subQ0=sQuery(id+"F18.wireOp",EDGE,"E27.44.1");Q6=makeQuery(id+"F18.imprint","IMPRINT",FACE,{"disambiguationData":[TD([[makeQuery(id+"F18.imprint","IMPRINT",EDGE,{"derivedFrom":subQ0}),1.0]])]});}
            var Q7;
            {var subQ0=sQuery(id+"F18.wireOp",EDGE,"E27.45.1");Q7=makeQuery(id+"F18.imprint","IMPRINT",FACE,{"disambiguationData":[TD([[makeQuery(id+"F18.imprint","IMPRINT",EDGE,{"derivedFrom":subQ0}),1.0]])]});}
            var Q8;
            {var subQ0=sQuery(id+"F18.wireOp",EDGE,"E27.46.1");Q8=makeQuery(id+"F18.imprint","IMPRINT",FACE,{"disambiguationData":[TD([[makeQuery(id+"F18.imprint","IMPRINT",EDGE,{"derivedFrom":subQ0}),1.0]])]});}
            var Q9;
            {var subQ0=sQuery(id+"F18.wireOp",EDGE,"E27.47.1");Q9=makeQuery(id+"F18.imprint","IMPRINT",FACE,{"disambiguationData":[TD([[makeQuery(id+"F18.imprint","IMPRINT",EDGE,{"derivedFrom":subQ0}),1.0]])]});}
            var Q10;
            {var subQ0=sQuery(id+"F18.wireOp",EDGE,"E27.48.1");Q10=makeQuery(id+"F18.imprint","IMPRINT",FACE,{"disambiguationData":[TD([[makeQuery(id+"F18.imprint","IMPRINT",EDGE,{"derivedFrom":subQ0}),1.0]])]});}
            var Q11;
            {var subQ0=sQuery(id+"F18.wireOp",EDGE,"E27.49.1");Q11=makeQuery(id+"F18.imprint","IMPRINT",FACE,{"disambiguationData":[TD([[makeQuery(id+"F18.imprint","IMPRINT",EDGE,{"derivedFrom":subQ0}),1.0]])]});}
            var Q12;
            {var subQ0=sQuery(id+"F18.wireOp",EDGE,"E25");Q12=makeQuery(id+"F18.imprint","IMPRINT",FACE,{"disambiguationData":[TD([[makeQuery(id+"F18.imprint","IMPRINT",EDGE,{"derivedFrom":subQ0}),1.0]])]});}
            var Q13;
            {var subQ0=sQuery(id+"F18.wireOp",EDGE,"E27.1.1");Q13=makeQuery(id+"F18.imprint","IMPRINT",FACE,{"disambiguationData":[TD([[makeQuery(id+"F18.imprint","IMPRINT",EDGE,{"derivedFrom":subQ0}),1.0]])]});}
            var Q14;
            {var subQ0=sQuery(id+"F18.wireOp",EDGE,"E27.2.1");Q14=makeQuery(id+"F18.imprint","IMPRINT",FACE,{"disambiguationData":[TD([[makeQuery(id+"F18.imprint","IMPRINT",EDGE,{"derivedFrom":subQ0}),1.0]])]});}
            var Q15;
            {var subQ0=sQuery(id+"F18.wireOp",EDGE,"E27.3.1");Q15=makeQuery(id+"F18.imprint","IMPRINT",FACE,{"disambiguationData":[TD([[makeQuery(id+"F18.imprint","IMPRINT",EDGE,{"derivedFrom":subQ0}),1.0]])]});}
            var Q16;
            {var subQ0=sQuery(id+"F18.wireOp",EDGE,"E27.4.1");Q16=makeQuery(id+"F18.imprint","IMPRINT",FACE,{"disambiguationData":[TD([[makeQuery(id+"F18.imprint","IMPRINT",EDGE,{"derivedFrom":subQ0}),1.0]])]});}
            var Q17;
            {var subQ0=sQuery(id+"F18.wireOp",EDGE,"E27.5.1");Q17=makeQuery(id+"F18.imprint","IMPRINT",FACE,{"disambiguationData":[TD([[makeQuery(id+"F18.imprint","IMPRINT",EDGE,{"derivedFrom":subQ0}),1.0]])]});}
            var Q18;
            {var subQ0=sQuery(id+"F18.wireOp",EDGE,"E27.6.1");Q18=makeQuery(id+"F18.imprint","IMPRINT",FACE,{"disambiguationData":[TD([[makeQuery(id+"F18.imprint","IMPRINT",EDGE,{"derivedFrom":subQ0}),1.0]])]});}
            var Q19;
            {var subQ0=sQuery(id+"F18.wireOp",EDGE,"E27.7.1");Q19=makeQuery(id+"F18.imprint","IMPRINT",FACE,{"disambiguationData":[TD([[makeQuery(id+"F18.imprint","IMPRINT",EDGE,{"derivedFrom":subQ0}),1.0]])]});}
            var Q20;
            {var subQ0=sQuery(id+"F18.wireOp",EDGE,"E27.8.1");Q20=makeQuery(id+"F18.imprint","IMPRINT",FACE,{"disambiguationData":[TD([[makeQuery(id+"F18.imprint","IMPRINT",EDGE,{"derivedFrom":subQ0}),1.0]])]});}
            var Q21;
            {var subQ0=sQuery(id+"F18.wireOp",EDGE,"E27.9.1");Q21=makeQuery(id+"F18.imprint","IMPRINT",FACE,{"disambiguationData":[TD([[makeQuery(id+"F18.imprint","IMPRINT",EDGE,{"derivedFrom":subQ0}),1.0]])]});}
            var Q22;
            {var subQ0=sQuery(id+"F18.wireOp",EDGE,"E27.10.1");Q22=makeQuery(id+"F18.imprint","IMPRINT",FACE,{"disambiguationData":[TD([[makeQuery(id+"F18.imprint","IMPRINT",EDGE,{"derivedFrom":subQ0}),1.0]])]});}
            var Q23;
            {var subQ0=sQuery(id+"F18.wireOp",EDGE,"E27.11.1");Q23=makeQuery(id+"F18.imprint","IMPRINT",FACE,{"disambiguationData":[TD([[makeQuery(id+"F18.imprint","IMPRINT",EDGE,{"derivedFrom":subQ0}),1.0]])]});}
            var Q24;
            {var subQ0=sQuery(id+"F18.wireOp",EDGE,"E27.12.1");Q24=makeQuery(id+"F18.imprint","IMPRINT",FACE,{"disambiguationData":[TD([[makeQuery(id+"F18.imprint","IMPRINT",EDGE,{"derivedFrom":subQ0}),1.0]])]});}
            var Q25;
            {var subQ0=sQuery(id+"F18.wireOp",EDGE,"E27.13.1");Q25=makeQuery(id+"F18.imprint","IMPRINT",FACE,{"disambiguationData":[TD([[makeQuery(id+"F18.imprint","IMPRINT",EDGE,{"derivedFrom":subQ0}),1.0]])]});}
            var Q26;
            {var subQ0=sQuery(id+"F18.wireOp",EDGE,"E27.14.1");Q26=makeQuery(id+"F18.imprint","IMPRINT",FACE,{"disambiguationData":[TD([[makeQuery(id+"F18.imprint","IMPRINT",EDGE,{"derivedFrom":subQ0}),1.0]])]});}
            var Q27;
            {var subQ0=sQuery(id+"F18.wireOp",EDGE,"E27.15.1");Q27=makeQuery(id+"F18.imprint","IMPRINT",FACE,{"disambiguationData":[TD([[makeQuery(id+"F18.imprint","IMPRINT",EDGE,{"derivedFrom":subQ0}),1.0]])]});}
            var Q28;
            {var subQ0=sQuery(id+"F18.wireOp",EDGE,"E27.16.1");Q28=makeQuery(id+"F18.imprint","IMPRINT",FACE,{"disambiguationData":[TD([[makeQuery(id+"F18.imprint","IMPRINT",EDGE,{"derivedFrom":subQ0}),1.0]])]});}
            var Q29;
            {var subQ0=sQuery(id+"F18.wireOp",EDGE,"E27.17.1");Q29=makeQuery(id+"F18.imprint","IMPRINT",FACE,{"disambiguationData":[TD([[makeQuery(id+"F18.imprint","IMPRINT",EDGE,{"derivedFrom":subQ0}),1.0]])]});}
            var Q30;
            {var subQ0=sQuery(id+"F18.wireOp",EDGE,"E27.18.1");Q30=makeQuery(id+"F18.imprint","IMPRINT",FACE,{"disambiguationData":[TD([[makeQuery(id+"F18.imprint","IMPRINT",EDGE,{"derivedFrom":subQ0}),1.0]])]});}
            var Q31;
            {var subQ0=sQuery(id+"F18.wireOp",EDGE,"E27.19.1");Q31=makeQuery(id+"F18.imprint","IMPRINT",FACE,{"disambiguationData":[TD([[makeQuery(id+"F18.imprint","IMPRINT",EDGE,{"derivedFrom":subQ0}),1.0]])]});}
            var Q32;
            {var subQ0=sQuery(id+"F18.wireOp",EDGE,"E27.20.1");Q32=makeQuery(id+"F18.imprint","IMPRINT",FACE,{"disambiguationData":[TD([[makeQuery(id+"F18.imprint","IMPRINT",EDGE,{"derivedFrom":subQ0}),1.0]])]});}
            var Q33;
            {var subQ0=sQuery(id+"F18.wireOp",EDGE,"E27.21.1");Q33=makeQuery(id+"F18.imprint","IMPRINT",FACE,{"disambiguationData":[TD([[makeQuery(id+"F18.imprint","IMPRINT",EDGE,{"derivedFrom":subQ0}),1.0]])]});}
            var Q34;
            {var subQ0=sQuery(id+"F18.wireOp",EDGE,"E27.22.1");Q34=makeQuery(id+"F18.imprint","IMPRINT",FACE,{"disambiguationData":[TD([[makeQuery(id+"F18.imprint","IMPRINT",EDGE,{"derivedFrom":subQ0}),1.0]])]});}
            var Q35;
            {var subQ0=sQuery(id+"F18.wireOp",EDGE,"E27.23.1");Q35=makeQuery(id+"F18.imprint","IMPRINT",FACE,{"disambiguationData":[TD([[makeQuery(id+"F18.imprint","IMPRINT",EDGE,{"derivedFrom":subQ0}),1.0]])]});}
            var Q36;
            {var subQ0=sQuery(id+"F18.wireOp",EDGE,"E27.24.1");Q36=makeQuery(id+"F18.imprint","IMPRINT",FACE,{"disambiguationData":[TD([[makeQuery(id+"F18.imprint","IMPRINT",EDGE,{"derivedFrom":subQ0}),1.0]])]});}
            var Q37;
            {var subQ0=sQuery(id+"F18.wireOp",EDGE,"E27.25.1");Q37=makeQuery(id+"F18.imprint","IMPRINT",FACE,{"disambiguationData":[TD([[makeQuery(id+"F18.imprint","IMPRINT",EDGE,{"derivedFrom":subQ0}),1.0]])]});}
            var Q38;
            {var subQ0=sQuery(id+"F18.wireOp",EDGE,"E27.26.1");Q38=makeQuery(id+"F18.imprint","IMPRINT",FACE,{"disambiguationData":[TD([[makeQuery(id+"F18.imprint","IMPRINT",EDGE,{"derivedFrom":subQ0}),1.0]])]});}
            var Q39;
            {var subQ0=sQuery(id+"F18.wireOp",EDGE,"E27.27.1");Q39=makeQuery(id+"F18.imprint","IMPRINT",FACE,{"disambiguationData":[TD([[makeQuery(id+"F18.imprint","IMPRINT",EDGE,{"derivedFrom":subQ0}),1.0]])]});}
            var Q40;
            {var subQ0=sQuery(id+"F18.wireOp",EDGE,"E27.28.1");Q40=makeQuery(id+"F18.imprint","IMPRINT",FACE,{"disambiguationData":[TD([[makeQuery(id+"F18.imprint","IMPRINT",EDGE,{"derivedFrom":subQ0}),1.0]])]});}
            var Q41;
            {var subQ0=sQuery(id+"F18.wireOp",EDGE,"E27.29.1");Q41=makeQuery(id+"F18.imprint","IMPRINT",FACE,{"disambiguationData":[TD([[makeQuery(id+"F18.imprint","IMPRINT",EDGE,{"derivedFrom":subQ0}),1.0]])]});}
            var Q42;
            {var subQ0=sQuery(id+"F18.wireOp",EDGE,"E27.30.1");Q42=makeQuery(id+"F18.imprint","IMPRINT",FACE,{"disambiguationData":[TD([[makeQuery(id+"F18.imprint","IMPRINT",EDGE,{"derivedFrom":subQ0}),1.0]])]});}
            var Q43;
            {var subQ0=sQuery(id+"F18.wireOp",EDGE,"E27.31.1");Q43=makeQuery(id+"F18.imprint","IMPRINT",FACE,{"disambiguationData":[TD([[makeQuery(id+"F18.imprint","IMPRINT",EDGE,{"derivedFrom":subQ0}),1.0]])]});}
            var Q44;
            {var subQ0=sQuery(id+"F18.wireOp",EDGE,"E27.32.1");Q44=makeQuery(id+"F18.imprint","IMPRINT",FACE,{"disambiguationData":[TD([[makeQuery(id+"F18.imprint","IMPRINT",EDGE,{"derivedFrom":subQ0}),1.0]])]});}
            var Q45;
            {var subQ0=sQuery(id+"F18.wireOp",EDGE,"E27.33.1");Q45=makeQuery(id+"F18.imprint","IMPRINT",FACE,{"disambiguationData":[TD([[makeQuery(id+"F18.imprint","IMPRINT",EDGE,{"derivedFrom":subQ0}),1.0]])]});}
            var Q46;
            {var subQ0=sQuery(id+"F18.wireOp",EDGE,"E27.34.1");Q46=makeQuery(id+"F18.imprint","IMPRINT",FACE,{"disambiguationData":[TD([[makeQuery(id+"F18.imprint","IMPRINT",EDGE,{"derivedFrom":subQ0}),1.0]])]});}
            var Q47;
            {var subQ0=sQuery(id+"F18.wireOp",EDGE,"E27.35.1");Q47=makeQuery(id+"F18.imprint","IMPRINT",FACE,{"disambiguationData":[TD([[makeQuery(id+"F18.imprint","IMPRINT",EDGE,{"derivedFrom":subQ0}),1.0]])]});}
            var Q48;
            {var subQ0=sQuery(id+"F18.wireOp",EDGE,"E27.36.1");Q48=makeQuery(id+"F18.imprint","IMPRINT",FACE,{"disambiguationData":[TD([[makeQuery(id+"F18.imprint","IMPRINT",EDGE,{"derivedFrom":subQ0}),1.0]])]});}
            var Q49;
            {var subQ0=sQuery(id+"F18.wireOp",EDGE,"E27.37.1");Q49=makeQuery(id+"F18.imprint","IMPRINT",FACE,{"disambiguationData":[TD([[makeQuery(id+"F18.imprint","IMPRINT",EDGE,{"derivedFrom":subQ0}),1.0]])]});}
            var Q50;
            Q50=makeQuery(id+"F18.imprint","IMPRINT",FACE,{"disambiguationData":[TD([[makeQuery(id+"F18.imprint","IMPRINT",EDGE,{"derivedFrom":makeQuery(id+"F7.opExtrude","CAP_EDGE",EDGE,{"disambiguationData":[OSD([sQuery(id+"F6.wireOp",EDGE,"E11")])],"isStart":true})}),-1.0]])]});
            var Q51;
            Q51=makeQuery(id+"F18.imprint","IMPRINT",FACE,{"disambiguationData":[TD([[makeQuery(id+"F18.imprint","IMPRINT",EDGE,{"derivedFrom":sQuery(id+"F18.wireOp",EDGE,"E24")}),-1.0]])]});
            extrude(context, id + "F19", {"entities" : qUnion([Q0, Q1, Q2, Q3, Q4, Q5, Q6, Q7, Q8, Q9, Q10, Q11, Q12, Q13, Q14, Q15, Q16, Q17, Q18, Q19, Q20, Q21, Q22, Q23, Q24, Q25, Q26, Q27, Q28, Q29, Q30, Q31, Q32, Q33, Q34, Q35, Q36, Q37, Q38, Q39, Q40, Q41, Q42, Q43, Q44, Q45, Q46, Q47, Q48, Q49, Q50, Q51]), "operationType" : NewBodyOperationType.ADD, "depth" : 6.35 * mm});
        }
        {
            var Q0;
            Q0=makeQuery(id+"F19.opExtrude","CAP_FACE",FACE,{"disambiguationData":[OSD([sQuery(id+"F18.wireOp",EDGE,"E21"),sQuery(id+"F18.wireOp",EDGE,"E24"),sQuery(id+"F18.wireOp",EDGE,"E26"),sQuery(id+"F18.wireOp",EDGE,"E27.1.0"),sQuery(id+"F18.wireOp",EDGE,"E27.1.2"),sQuery(id+"F18.wireOp",EDGE,"E27.2.0"),sQuery(id+"F18.wireOp",EDGE,"E27.2.2"),sQuery(id+"F18.wireOp",EDGE,"E27.3.0"),sQuery(id+"F18.wireOp",EDGE,"E27.3.2"),sQuery(id+"F18.wireOp",EDGE,"E27.4.0"),sQuery(id+"F18.wireOp",EDGE,"E27.4.2"),sQuery(id+"F18.wireOp",EDGE,"E27.5.0"),sQuery(id+"F18.wireOp",EDGE,"E27.5.2"),sQuery(id+"F18.wireOp",EDGE,"E27.6.0"),sQuery(id+"F18.wireOp",EDGE,"E27.6.2"),sQuery(id+"F18.wireOp",EDGE,"E27.7.0"),sQuery(id+"F18.wireOp",EDGE,"E27.7.2"),sQuery(id+"F18.wireOp",EDGE,"E27.8.0"),sQuery(id+"F18.wireOp",EDGE,"E27.8.2"),sQuery(id+"F18.wireOp",EDGE,"E27.9.0"),sQuery(id+"F18.wireOp",EDGE,"E27.9.2"),sQuery(id+"F18.wireOp",EDGE,"E27.10.0"),sQuery(id+"F18.wireOp",EDGE,"E27.10.2"),sQuery(id+"F18.wireOp",EDGE,"E27.11.0"),sQuery(id+"F18.wireOp",EDGE,"E27.11.2"),sQuery(id+"F18.wireOp",EDGE,"E27.12.0"),sQuery(id+"F18.wireOp",EDGE,"E27.12.2"),sQuery(id+"F18.wireOp",EDGE,"E27.13.0"),sQuery(id+"F18.wireOp",EDGE,"E27.13.2"),sQuery(id+"F18.wireOp",EDGE,"E27.14.0"),sQuery(id+"F18.wireOp",EDGE,"E27.14.2"),sQuery(id+"F18.wireOp",EDGE,"E27.15.0"),sQuery(id+"F18.wireOp",EDGE,"E27.15.2"),sQuery(id+"F18.wireOp",EDGE,"E27.16.0"),sQuery(id+"F18.wireOp",EDGE,"E27.16.2"),sQuery(id+"F18.wireOp",EDGE,"E27.17.0"),sQuery(id+"F18.wireOp",EDGE,"E27.17.2"),sQuery(id+"F18.wireOp",EDGE,"E27.18.0"),sQuery(id+"F18.wireOp",EDGE,"E27.18.2"),sQuery(id+"F18.wireOp",EDGE,"E27.19.0"),sQuery(id+"F18.wireOp",EDGE,"E27.19.2"),sQuery(id+"F18.wireOp",EDGE,"E27.20.0"),sQuery(id+"F18.wireOp",EDGE,"E27.20.2"),sQuery(id+"F18.wireOp",EDGE,"E27.21.0"),sQuery(id+"F18.wireOp",EDGE,"E27.21.2"),sQuery(id+"F18.wireOp",EDGE,"E27.22.0"),sQuery(id+"F18.wireOp",EDGE,"E27.22.2"),sQuery(id+"F18.wireOp",EDGE,"E27.23.0"),sQuery(id+"F18.wireOp",EDGE,"E27.23.2"),sQuery(id+"F18.wireOp",EDGE,"E27.24.0"),sQuery(id+"F18.wireOp",EDGE,"E27.24.2"),sQuery(id+"F18.wireOp",EDGE,"E27.25.0"),sQuery(id+"F18.wireOp",EDGE,"E27.25.2"),sQuery(id+"F18.wireOp",EDGE,"E27.26.0"),sQuery(id+"F18.wireOp",EDGE,"E27.26.2"),sQuery(id+"F18.wireOp",EDGE,"E27.27.0"),sQuery(id+"F18.wireOp",EDGE,"E27.27.2"),sQuery(id+"F18.wireOp",EDGE,"E27.28.0"),sQuery(id+"F18.wireOp",EDGE,"E27.28.2"),sQuery(id+"F18.wireOp",EDGE,"E27.29.0"),sQuery(id+"F18.wireOp",EDGE,"E27.29.2"),sQuery(id+"F18.wireOp",EDGE,"E27.30.0"),sQuery(id+"F18.wireOp",EDGE,"E27.30.2"),sQuery(id+"F18.wireOp",EDGE,"E27.31.0"),sQuery(id+"F18.wireOp",EDGE,"E27.31.2"),sQuery(id+"F18.wireOp",EDGE,"E27.32.0"),sQuery(id+"F18.wireOp",EDGE,"E27.32.2"),sQuery(id+"F18.wireOp",EDGE,"E27.33.0"),sQuery(id+"F18.wireOp",EDGE,"E27.33.2"),sQuery(id+"F18.wireOp",EDGE,"E27.34.0"),sQuery(id+"F18.wireOp",EDGE,"E27.34.2"),sQuery(id+"F18.wireOp",EDGE,"E27.35.0"),sQuery(id+"F18.wireOp",EDGE,"E27.35.2"),sQuery(id+"F18.wireOp",EDGE,"E27.36.0"),sQuery(id+"F18.wireOp",EDGE,"E27.36.2"),sQuery(id+"F18.wireOp",EDGE,"E27.37.0"),sQuery(id+"F18.wireOp",EDGE,"E27.37.2"),sQuery(id+"F18.wireOp",EDGE,"E27.38.0"),sQuery(id+"F18.wireOp",EDGE,"E27.38.2"),sQuery(id+"F18.wireOp",EDGE,"E27.39.0"),sQuery(id+"F18.wireOp",EDGE,"E27.39.2"),sQuery(id+"F18.wireOp",EDGE,"E27.40.0"),sQuery(id+"F18.wireOp",EDGE,"E27.40.2"),sQuery(id+"F18.wireOp",EDGE,"E27.41.0"),sQuery(id+"F18.wireOp",EDGE,"E27.41.2"),sQuery(id+"F18.wireOp",EDGE,"E27.42.0"),sQuery(id+"F18.wireOp",EDGE,"E27.42.2"),sQuery(id+"F18.wireOp",EDGE,"E27.43.0"),sQuery(id+"F18.wireOp",EDGE,"E27.43.2"),sQuery(id+"F18.wireOp",EDGE,"E27.44.0"),sQuery(id+"F18.wireOp",EDGE,"E27.44.2"),sQuery(id+"F18.wireOp",EDGE,"E27.45.0"),sQuery(id+"F18.wireOp",EDGE,"E27.45.2"),sQuery(id+"F18.wireOp",EDGE,"E27.46.0"),sQuery(id+"F18.wireOp",EDGE,"E27.46.2"),sQuery(id+"F18.wireOp",EDGE,"E27.47.0"),sQuery(id+"F18.wireOp",EDGE,"E27.47.2"),sQuery(id+"F18.wireOp",EDGE,"E27.48.0"),sQuery(id+"F18.wireOp",EDGE,"E27.48.2"),sQuery(id+"F18.wireOp",EDGE,"E27.49.0"),sQuery(id+"F18.wireOp",EDGE,"E27.49.2"),sQuery(id+"F18.wireOp",EDGE,"E28"),sQuery(id+"F18.wireOp",EDGE,"E29.1.0"),sQuery(id+"F18.wireOp",EDGE,"E29.2.0"),sQuery(id+"F18.wireOp",EDGE,"E29.3.0"),sQuery(id+"F18.wireOp",EDGE,"E29.4.0"),sQuery(id+"F18.wireOp",EDGE,"E29.5.0"),sQuery(id+"F18.wireOp",EDGE,"E29.6.0"),sQuery(id+"F18.wireOp",EDGE,"E29.7.0"),sQuery(id+"F18.wireOp",EDGE,"E29.8.0"),sQuery(id+"F18.wireOp",EDGE,"E29.9.0"),sQuery(id+"F18.wireOp",EDGE,"E29.10.0"),sQuery(id+"F18.wireOp",EDGE,"E29.11.0"),sQuery(id+"F18.wireOp",EDGE,"E29.12.0"),sQuery(id+"F18.wireOp",EDGE,"E29.13.0"),sQuery(id+"F18.wireOp",EDGE,"E29.14.0"),sQuery(id+"F18.wireOp",EDGE,"E29.15.0"),sQuery(id+"F18.wireOp",EDGE,"E29.16.0"),sQuery(id+"F18.wireOp",EDGE,"E29.17.0"),sQuery(id+"F18.wireOp",EDGE,"E29.18.0"),sQuery(id+"F18.wireOp",EDGE,"E29.19.0"),sQuery(id+"F18.wireOp",EDGE,"E29.20.0"),sQuery(id+"F18.wireOp",EDGE,"E29.21.0"),sQuery(id+"F18.wireOp",EDGE,"E29.22.0"),sQuery(id+"F18.wireOp",EDGE,"E29.23.0"),sQuery(id+"F18.wireOp",EDGE,"E29.24.0"),sQuery(id+"F18.wireOp",EDGE,"E29.25.0"),sQuery(id+"F18.wireOp",EDGE,"E29.26.0"),sQuery(id+"F18.wireOp",EDGE,"E29.27.0"),sQuery(id+"F18.wireOp",EDGE,"E29.28.0"),sQuery(id+"F18.wireOp",EDGE,"E29.29.0"),sQuery(id+"F18.wireOp",EDGE,"E29.30.0"),sQuery(id+"F18.wireOp",EDGE,"E29.31.0"),sQuery(id+"F18.wireOp",EDGE,"E29.32.0"),sQuery(id+"F18.wireOp",EDGE,"E29.33.0"),sQuery(id+"F18.wireOp",EDGE,"E29.34.0"),sQuery(id+"F18.wireOp",EDGE,"E29.35.0"),sQuery(id+"F18.wireOp",EDGE,"E29.36.0"),sQuery(id+"F18.wireOp",EDGE,"E29.37.0"),sQuery(id+"F18.wireOp",EDGE,"E29.38.0"),sQuery(id+"F18.wireOp",EDGE,"E29.39.0"),sQuery(id+"F18.wireOp",EDGE,"E29.40.0"),sQuery(id+"F18.wireOp",EDGE,"E29.41.0"),sQuery(id+"F18.wireOp",EDGE,"E29.42.0"),sQuery(id+"F18.wireOp",EDGE,"E29.43.0"),sQuery(id+"F18.wireOp",EDGE,"E29.44.0"),sQuery(id+"F18.wireOp",EDGE,"E29.45.0"),sQuery(id+"F18.wireOp",EDGE,"E29.46.0"),sQuery(id+"F18.wireOp",EDGE,"E29.47.0"),sQuery(id+"F18.wireOp",EDGE,"E29.48.0"),sQuery(id+"F18.wireOp",EDGE,"E29.49.0")])],"isStart":false});
            var sketch = newSketch(context, id + "F20", { "sketchPlane" : qUnion([Q0])});
            skCircle(sketch, "E30", {"center": v(-23.99, -14.32) * mm, "radius": 2.51 * mm});
            skLineSegment(sketch, "E31", {"start": v(-23.99, -14.32) * mm, "end": v(-23.99, -11.15) * mm});
            skLineSegment(sketch, "E32", {"start": v(-24.62, -11.21) * mm, "end": v(-24.75, -11.93) * mm});
            skLineSegment(sketch, "E33", {"start": v(-23.35, -11.21) * mm, "end": v(-23.23, -11.93) * mm});
            skLineSegment(sketch, "E34", {"start": v(-24.62, -11.21) * mm, "end": v(-23.35, -11.21) * mm});
            skLineSegment(sketch, "E35.1.0", {"start": v(-27.14, -13.97) * mm, "end": v(-26.5, -14.3) * mm});
            skLineSegment(sketch, "E35.1.1", {"start": v(-27.14, -13.97) * mm, "end": v(-26.75, -12.76) * mm});
            skLineSegment(sketch, "E35.1.2", {"start": v(-26.75, -12.76) * mm, "end": v(-26.03, -12.86) * mm});
            skLineSegment(sketch, "E35.2.0", {"start": v(-25.3, -17.21) * mm, "end": v(-24.78, -16.7) * mm});
            skLineSegment(sketch, "E35.2.1", {"start": v(-25.3, -17.21) * mm, "end": v(-26.33, -16.47) * mm});
            skLineSegment(sketch, "E35.2.2", {"start": v(-26.33, -16.47) * mm, "end": v(-26.01, -15.81) * mm});
            skLineSegment(sketch, "E35.3.0", {"start": v(-21.65, -16.47) * mm, "end": v(-21.96, -15.81) * mm});
            skLineSegment(sketch, "E35.3.1", {"start": v(-21.65, -16.47) * mm, "end": v(-22.67, -17.21) * mm});
            skLineSegment(sketch, "E35.3.2", {"start": v(-22.67, -17.21) * mm, "end": v(-23.2, -16.7) * mm});
            skLineSegment(sketch, "E35.4.0", {"start": v(-21.23, -12.76) * mm, "end": v(-21.95, -12.86) * mm});
            skLineSegment(sketch, "E35.4.1", {"start": v(-21.23, -12.76) * mm, "end": v(-20.83, -13.97) * mm});
            skLineSegment(sketch, "E35.4.2", {"start": v(-20.83, -13.97) * mm, "end": v(-21.48, -14.3) * mm});
            skSolve(sketch);
        }
        {
            var Q0;
            Q0 = qSketchRegion(id + "F20", true);
            extrude(context, id + "F21", {"entities" : qUnion([Q0]), "operationType" : NewBodyOperationType.ADD, "oppositeDirection" : true, "depth" : 6.35 * mm});
        }
        {
            var Q0;
            Q0=makeQuery(id+"F21.boolean.opBoolean","MERGE",FACE,{"derivedFrom":[makeQuery(id+"F19.opExtrude","CAP_FACE",FACE,{"disambiguationData":[OSD([sQuery(id+"F18.wireOp",EDGE,"E21"),sQuery(id+"F18.wireOp",EDGE,"E24"),sQuery(id+"F18.wireOp",EDGE,"E26"),sQuery(id+"F18.wireOp",EDGE,"E27.1.0"),sQuery(id+"F18.wireOp",EDGE,"E27.1.2"),sQuery(id+"F18.wireOp",EDGE,"E27.2.0"),sQuery(id+"F18.wireOp",EDGE,"E27.2.2"),sQuery(id+"F18.wireOp",EDGE,"E27.3.0"),sQuery(id+"F18.wireOp",EDGE,"E27.3.2"),sQuery(id+"F18.wireOp",EDGE,"E27.4.0"),sQuery(id+"F18.wireOp",EDGE,"E27.4.2"),sQuery(id+"F18.wireOp",EDGE,"E27.5.0"),sQuery(id+"F18.wireOp",EDGE,"E27.5.2"),sQuery(id+"F18.wireOp",EDGE,"E27.6.0"),sQuery(id+"F18.wireOp",EDGE,"E27.6.2"),sQuery(id+"F18.wireOp",EDGE,"E27.7.0"),sQuery(id+"F18.wireOp",EDGE,"E27.7.2"),sQuery(id+"F18.wireOp",EDGE,"E27.8.0"),sQuery(id+"F18.wireOp",EDGE,"E27.8.2"),sQuery(id+"F18.wireOp",EDGE,"E27.9.0"),sQuery(id+"F18.wireOp",EDGE,"E27.9.2"),sQuery(id+"F18.wireOp",EDGE,"E27.10.0"),sQuery(id+"F18.wireOp",EDGE,"E27.10.2"),sQuery(id+"F18.wireOp",EDGE,"E27.11.0"),sQuery(id+"F18.wireOp",EDGE,"E27.11.2"),sQuery(id+"F18.wireOp",EDGE,"E27.12.0"),sQuery(id+"F18.wireOp",EDGE,"E27.12.2"),sQuery(id+"F18.wireOp",EDGE,"E27.13.0"),sQuery(id+"F18.wireOp",EDGE,"E27.13.2"),sQuery(id+"F18.wireOp",EDGE,"E27.14.0"),sQuery(id+"F18.wireOp",EDGE,"E27.14.2"),sQuery(id+"F18.wireOp",EDGE,"E27.15.0"),sQuery(id+"F18.wireOp",EDGE,"E27.15.2"),sQuery(id+"F18.wireOp",EDGE,"E27.16.0"),sQuery(id+"F18.wireOp",EDGE,"E27.16.2"),sQuery(id+"F18.wireOp",EDGE,"E27.17.0"),sQuery(id+"F18.wireOp",EDGE,"E27.17.2"),sQuery(id+"F18.wireOp",EDGE,"E27.18.0"),sQuery(id+"F18.wireOp",EDGE,"E27.18.2"),sQuery(id+"F18.wireOp",EDGE,"E27.19.0"),sQuery(id+"F18.wireOp",EDGE,"E27.19.2"),sQuery(id+"F18.wireOp",EDGE,"E27.20.0"),sQuery(id+"F18.wireOp",EDGE,"E27.20.2"),sQuery(id+"F18.wireOp",EDGE,"E27.21.0"),sQuery(id+"F18.wireOp",EDGE,"E27.21.2"),sQuery(id+"F18.wireOp",EDGE,"E27.22.0"),sQuery(id+"F18.wireOp",EDGE,"E27.22.2"),sQuery(id+"F18.wireOp",EDGE,"E27.23.0"),sQuery(id+"F18.wireOp",EDGE,"E27.23.2"),sQuery(id+"F18.wireOp",EDGE,"E27.24.0"),sQuery(id+"F18.wireOp",EDGE,"E27.24.2"),sQuery(id+"F18.wireOp",EDGE,"E27.25.0"),sQuery(id+"F18.wireOp",EDGE,"E27.25.2"),sQuery(id+"F18.wireOp",EDGE,"E27.26.0"),sQuery(id+"F18.wireOp",EDGE,"E27.26.2"),sQuery(id+"F18.wireOp",EDGE,"E27.27.0"),sQuery(id+"F18.wireOp",EDGE,"E27.27.2"),sQuery(id+"F18.wireOp",EDGE,"E27.28.0"),sQuery(id+"F18.wireOp",EDGE,"E27.28.2"),sQuery(id+"F18.wireOp",EDGE,"E27.29.0"),sQuery(id+"F18.wireOp",EDGE,"E27.29.2"),sQuery(id+"F18.wireOp",EDGE,"E27.30.0"),sQuery(id+"F18.wireOp",EDGE,"E27.30.2"),sQuery(id+"F18.wireOp",EDGE,"E27.31.0"),sQuery(id+"F18.wireOp",EDGE,"E27.31.2"),sQuery(id+"F18.wireOp",EDGE,"E27.32.0"),sQuery(id+"F18.wireOp",EDGE,"E27.32.2"),sQuery(id+"F18.wireOp",EDGE,"E27.33.0"),sQuery(id+"F18.wireOp",EDGE,"E27.33.2"),sQuery(id+"F18.wireOp",EDGE,"E27.34.0"),sQuery(id+"F18.wireOp",EDGE,"E27.34.2"),sQuery(id+"F18.wireOp",EDGE,"E27.35.0"),sQuery(id+"F18.wireOp",EDGE,"E27.35.2"),sQuery(id+"F18.wireOp",EDGE,"E27.36.0"),sQuery(id+"F18.wireOp",EDGE,"E27.36.2"),sQuery(id+"F18.wireOp",EDGE,"E27.37.0"),sQuery(id+"F18.wireOp",EDGE,"E27.37.2"),sQuery(id+"F18.wireOp",EDGE,"E27.38.0"),sQuery(id+"F18.wireOp",EDGE,"E27.38.2"),sQuery(id+"F18.wireOp",EDGE,"E27.39.0"),sQuery(id+"F18.wireOp",EDGE,"E27.39.2"),sQuery(id+"F18.wireOp",EDGE,"E27.40.0"),sQuery(id+"F18.wireOp",EDGE,"E27.40.2"),sQuery(id+"F18.wireOp",EDGE,"E27.41.0"),sQuery(id+"F18.wireOp",EDGE,"E27.41.2"),sQuery(id+"F18.wireOp",EDGE,"E27.42.0"),sQuery(id+"F18.wireOp",EDGE,"E27.42.2"),sQuery(id+"F18.wireOp",EDGE,"E27.43.0"),sQuery(id+"F18.wireOp",EDGE,"E27.43.2"),sQuery(id+"F18.wireOp",EDGE,"E27.44.0"),sQuery(id+"F18.wireOp",EDGE,"E27.44.2"),sQuery(id+"F18.wireOp",EDGE,"E27.45.0"),sQuery(id+"F18.wireOp",EDGE,"E27.45.2"),sQuery(id+"F18.wireOp",EDGE,"E27.46.0"),sQuery(id+"F18.wireOp",EDGE,"E27.46.2"),sQuery(id+"F18.wireOp",EDGE,"E27.47.0"),sQuery(id+"F18.wireOp",EDGE,"E27.47.2"),sQuery(id+"F18.wireOp",EDGE,"E27.48.0"),sQuery(id+"F18.wireOp",EDGE,"E27.48.2"),sQuery(id+"F18.wireOp",EDGE,"E27.49.0"),sQuery(id+"F18.wireOp",EDGE,"E27.49.2"),sQuery(id+"F18.wireOp",EDGE,"E28"),sQuery(id+"F18.wireOp",EDGE,"E29.1.0"),sQuery(id+"F18.wireOp",EDGE,"E29.2.0"),sQuery(id+"F18.wireOp",EDGE,"E29.3.0"),sQuery(id+"F18.wireOp",EDGE,"E29.4.0"),sQuery(id+"F18.wireOp",EDGE,"E29.5.0"),sQuery(id+"F18.wireOp",EDGE,"E29.6.0"),sQuery(id+"F18.wireOp",EDGE,"E29.7.0"),sQuery(id+"F18.wireOp",EDGE,"E29.8.0"),sQuery(id+"F18.wireOp",EDGE,"E29.9.0"),sQuery(id+"F18.wireOp",EDGE,"E29.10.0"),sQuery(id+"F18.wireOp",EDGE,"E29.11.0"),sQuery(id+"F18.wireOp",EDGE,"E29.12.0"),sQuery(id+"F18.wireOp",EDGE,"E29.13.0"),sQuery(id+"F18.wireOp",EDGE,"E29.14.0"),sQuery(id+"F18.wireOp",EDGE,"E29.15.0"),sQuery(id+"F18.wireOp",EDGE,"E29.16.0"),sQuery(id+"F18.wireOp",EDGE,"E29.17.0"),sQuery(id+"F18.wireOp",EDGE,"E29.18.0"),sQuery(id+"F18.wireOp",EDGE,"E29.19.0"),sQuery(id+"F18.wireOp",EDGE,"E29.20.0"),sQuery(id+"F18.wireOp",EDGE,"E29.21.0"),sQuery(id+"F18.wireOp",EDGE,"E29.22.0"),sQuery(id+"F18.wireOp",EDGE,"E29.23.0"),sQuery(id+"F18.wireOp",EDGE,"E29.24.0"),sQuery(id+"F18.wireOp",EDGE,"E29.25.0"),sQuery(id+"F18.wireOp",EDGE,"E29.26.0"),sQuery(id+"F18.wireOp",EDGE,"E29.27.0"),sQuery(id+"F18.wireOp",EDGE,"E29.28.0"),sQuery(id+"F18.wireOp",EDGE,"E29.29.0"),sQuery(id+"F18.wireOp",EDGE,"E29.30.0"),sQuery(id+"F18.wireOp",EDGE,"E29.31.0"),sQuery(id+"F18.wireOp",EDGE,"E29.32.0"),sQuery(id+"F18.wireOp",EDGE,"E29.33.0"),sQuery(id+"F18.wireOp",EDGE,"E29.34.0"),sQuery(id+"F18.wireOp",EDGE,"E29.35.0"),sQuery(id+"F18.wireOp",EDGE,"E29.36.0"),sQuery(id+"F18.wireOp",EDGE,"E29.37.0"),sQuery(id+"F18.wireOp",EDGE,"E29.38.0"),sQuery(id+"F18.wireOp",EDGE,"E29.39.0"),sQuery(id+"F18.wireOp",EDGE,"E29.40.0"),sQuery(id+"F18.wireOp",EDGE,"E29.41.0"),sQuery(id+"F18.wireOp",EDGE,"E29.42.0"),sQuery(id+"F18.wireOp",EDGE,"E29.43.0"),sQuery(id+"F18.wireOp",EDGE,"E29.44.0"),sQuery(id+"F18.wireOp",EDGE,"E29.45.0"),sQuery(id+"F18.wireOp",EDGE,"E29.46.0"),sQuery(id+"F18.wireOp",EDGE,"E29.47.0"),sQuery(id+"F18.wireOp",EDGE,"E29.48.0"),sQuery(id+"F18.wireOp",EDGE,"E29.49.0")])],"isStart":false}),makeQuery(id+"F21.opExtrude","CAP_FACE",FACE,{"disambiguationData":[OSD([sQuery(id+"F20.wireOp",EDGE,"E30"),sQuery(id+"F20.wireOp",EDGE,"E32"),sQuery(id+"F20.wireOp",EDGE,"E33"),sQuery(id+"F20.wireOp",EDGE,"E34"),sQuery(id+"F20.wireOp",EDGE,"E35.1.0"),sQuery(id+"F20.wireOp",EDGE,"E35.1.1"),sQuery(id+"F20.wireOp",EDGE,"E35.1.2"),sQuery(id+"F20.wireOp",EDGE,"E35.2.0"),sQuery(id+"F20.wireOp",EDGE,"E35.2.1"),sQuery(id+"F20.wireOp",EDGE,"E35.2.2"),sQuery(id+"F20.wireOp",EDGE,"E35.3.0"),sQuery(id+"F20.wireOp",EDGE,"E35.3.1"),sQuery(id+"F20.wireOp",EDGE,"E35.3.2"),sQuery(id+"F20.wireOp",EDGE,"E35.4.0"),sQuery(id+"F20.wireOp",EDGE,"E35.4.1"),sQuery(id+"F20.wireOp",EDGE,"E35.4.2")])],"isStart":true})]});
            var sketch = newSketch(context, id + "F22", { "sketchPlane" : qUnion([Q0])});
            skCircle(sketch, "E36", {"center": v(-23.99, -14.32) * mm, "radius": 0.72 * mm});
            skSolve(sketch);
        }
        {
            var Q0;
            Q0=makeQuery(id+"F22.imprint","IMPRINT",FACE,{"disambiguationData":[TD([[makeQuery(id+"F22.imprint","IMPRINT",EDGE,{"derivedFrom":sQuery(id+"F22.wireOp",EDGE,"E36")}),1.0]])]});
            extrude(context, id + "F23", {"entities" : qUnion([Q0]), "operationType" : NewBodyOperationType.ADD, "depth" : 25.4 * mm});
        }
        {
            var Q0;
            Q0=makeQuery(id+"F21.boolean.opBoolean","MERGE",FACE,{"derivedFrom":[makeQuery(id+"F19.opExtrude","CAP_FACE",FACE,{"disambiguationData":[OSD([sQuery(id+"F18.wireOp",EDGE,"E21"),sQuery(id+"F18.wireOp",EDGE,"E24"),sQuery(id+"F18.wireOp",EDGE,"E26"),sQuery(id+"F18.wireOp",EDGE,"E27.1.0"),sQuery(id+"F18.wireOp",EDGE,"E27.1.2"),sQuery(id+"F18.wireOp",EDGE,"E27.2.0"),sQuery(id+"F18.wireOp",EDGE,"E27.2.2"),sQuery(id+"F18.wireOp",EDGE,"E27.3.0"),sQuery(id+"F18.wireOp",EDGE,"E27.3.2"),sQuery(id+"F18.wireOp",EDGE,"E27.4.0"),sQuery(id+"F18.wireOp",EDGE,"E27.4.2"),sQuery(id+"F18.wireOp",EDGE,"E27.5.0"),sQuery(id+"F18.wireOp",EDGE,"E27.5.2"),sQuery(id+"F18.wireOp",EDGE,"E27.6.0"),sQuery(id+"F18.wireOp",EDGE,"E27.6.2"),sQuery(id+"F18.wireOp",EDGE,"E27.7.0"),sQuery(id+"F18.wireOp",EDGE,"E27.7.2"),sQuery(id+"F18.wireOp",EDGE,"E27.8.0"),sQuery(id+"F18.wireOp",EDGE,"E27.8.2"),sQuery(id+"F18.wireOp",EDGE,"E27.9.0"),sQuery(id+"F18.wireOp",EDGE,"E27.9.2"),sQuery(id+"F18.wireOp",EDGE,"E27.10.0"),sQuery(id+"F18.wireOp",EDGE,"E27.10.2"),sQuery(id+"F18.wireOp",EDGE,"E27.11.0"),sQuery(id+"F18.wireOp",EDGE,"E27.11.2"),sQuery(id+"F18.wireOp",EDGE,"E27.12.0"),sQuery(id+"F18.wireOp",EDGE,"E27.12.2"),sQuery(id+"F18.wireOp",EDGE,"E27.13.0"),sQuery(id+"F18.wireOp",EDGE,"E27.13.2"),sQuery(id+"F18.wireOp",EDGE,"E27.14.0"),sQuery(id+"F18.wireOp",EDGE,"E27.14.2"),sQuery(id+"F18.wireOp",EDGE,"E27.15.0"),sQuery(id+"F18.wireOp",EDGE,"E27.15.2"),sQuery(id+"F18.wireOp",EDGE,"E27.16.0"),sQuery(id+"F18.wireOp",EDGE,"E27.16.2"),sQuery(id+"F18.wireOp",EDGE,"E27.17.0"),sQuery(id+"F18.wireOp",EDGE,"E27.17.2"),sQuery(id+"F18.wireOp",EDGE,"E27.18.0"),sQuery(id+"F18.wireOp",EDGE,"E27.18.2"),sQuery(id+"F18.wireOp",EDGE,"E27.19.0"),sQuery(id+"F18.wireOp",EDGE,"E27.19.2"),sQuery(id+"F18.wireOp",EDGE,"E27.20.0"),sQuery(id+"F18.wireOp",EDGE,"E27.20.2"),sQuery(id+"F18.wireOp",EDGE,"E27.21.0"),sQuery(id+"F18.wireOp",EDGE,"E27.21.2"),sQuery(id+"F18.wireOp",EDGE,"E27.22.0"),sQuery(id+"F18.wireOp",EDGE,"E27.22.2"),sQuery(id+"F18.wireOp",EDGE,"E27.23.0"),sQuery(id+"F18.wireOp",EDGE,"E27.23.2"),sQuery(id+"F18.wireOp",EDGE,"E27.24.0"),sQuery(id+"F18.wireOp",EDGE,"E27.24.2"),sQuery(id+"F18.wireOp",EDGE,"E27.25.0"),sQuery(id+"F18.wireOp",EDGE,"E27.25.2"),sQuery(id+"F18.wireOp",EDGE,"E27.26.0"),sQuery(id+"F18.wireOp",EDGE,"E27.26.2"),sQuery(id+"F18.wireOp",EDGE,"E27.27.0"),sQuery(id+"F18.wireOp",EDGE,"E27.27.2"),sQuery(id+"F18.wireOp",EDGE,"E27.28.0"),sQuery(id+"F18.wireOp",EDGE,"E27.28.2"),sQuery(id+"F18.wireOp",EDGE,"E27.29.0"),sQuery(id+"F18.wireOp",EDGE,"E27.29.2"),sQuery(id+"F18.wireOp",EDGE,"E27.30.0"),sQuery(id+"F18.wireOp",EDGE,"E27.30.2"),sQuery(id+"F18.wireOp",EDGE,"E27.31.0"),sQuery(id+"F18.wireOp",EDGE,"E27.31.2"),sQuery(id+"F18.wireOp",EDGE,"E27.32.0"),sQuery(id+"F18.wireOp",EDGE,"E27.32.2"),sQuery(id+"F18.wireOp",EDGE,"E27.33.0"),sQuery(id+"F18.wireOp",EDGE,"E27.33.2"),sQuery(id+"F18.wireOp",EDGE,"E27.34.0"),sQuery(id+"F18.wireOp",EDGE,"E27.34.2"),sQuery(id+"F18.wireOp",EDGE,"E27.35.0"),sQuery(id+"F18.wireOp",EDGE,"E27.35.2"),sQuery(id+"F18.wireOp",EDGE,"E27.36.0"),sQuery(id+"F18.wireOp",EDGE,"E27.36.2"),sQuery(id+"F18.wireOp",EDGE,"E27.37.0"),sQuery(id+"F18.wireOp",EDGE,"E27.37.2"),sQuery(id+"F18.wireOp",EDGE,"E27.38.0"),sQuery(id+"F18.wireOp",EDGE,"E27.38.2"),sQuery(id+"F18.wireOp",EDGE,"E27.39.0"),sQuery(id+"F18.wireOp",EDGE,"E27.39.2"),sQuery(id+"F18.wireOp",EDGE,"E27.40.0"),sQuery(id+"F18.wireOp",EDGE,"E27.40.2"),sQuery(id+"F18.wireOp",EDGE,"E27.41.0"),sQuery(id+"F18.wireOp",EDGE,"E27.41.2"),sQuery(id+"F18.wireOp",EDGE,"E27.42.0"),sQuery(id+"F18.wireOp",EDGE,"E27.42.2"),sQuery(id+"F18.wireOp",EDGE,"E27.43.0"),sQuery(id+"F18.wireOp",EDGE,"E27.43.2"),sQuery(id+"F18.wireOp",EDGE,"E27.44.0"),sQuery(id+"F18.wireOp",EDGE,"E27.44.2"),sQuery(id+"F18.wireOp",EDGE,"E27.45.0"),sQuery(id+"F18.wireOp",EDGE,"E27.45.2"),sQuery(id+"F18.wireOp",EDGE,"E27.46.0"),sQuery(id+"F18.wireOp",EDGE,"E27.46.2"),sQuery(id+"F18.wireOp",EDGE,"E27.47.0"),sQuery(id+"F18.wireOp",EDGE,"E27.47.2"),sQuery(id+"F18.wireOp",EDGE,"E27.48.0"),sQuery(id+"F18.wireOp",EDGE,"E27.48.2"),sQuery(id+"F18.wireOp",EDGE,"E27.49.0"),sQuery(id+"F18.wireOp",EDGE,"E27.49.2"),sQuery(id+"F18.wireOp",EDGE,"E28"),sQuery(id+"F18.wireOp",EDGE,"E29.1.0"),sQuery(id+"F18.wireOp",EDGE,"E29.2.0"),sQuery(id+"F18.wireOp",EDGE,"E29.3.0"),sQuery(id+"F18.wireOp",EDGE,"E29.4.0"),sQuery(id+"F18.wireOp",EDGE,"E29.5.0"),sQuery(id+"F18.wireOp",EDGE,"E29.6.0"),sQuery(id+"F18.wireOp",EDGE,"E29.7.0"),sQuery(id+"F18.wireOp",EDGE,"E29.8.0"),sQuery(id+"F18.wireOp",EDGE,"E29.9.0"),sQuery(id+"F18.wireOp",EDGE,"E29.10.0"),sQuery(id+"F18.wireOp",EDGE,"E29.11.0"),sQuery(id+"F18.wireOp",EDGE,"E29.12.0"),sQuery(id+"F18.wireOp",EDGE,"E29.13.0"),sQuery(id+"F18.wireOp",EDGE,"E29.14.0"),sQuery(id+"F18.wireOp",EDGE,"E29.15.0"),sQuery(id+"F18.wireOp",EDGE,"E29.16.0"),sQuery(id+"F18.wireOp",EDGE,"E29.17.0"),sQuery(id+"F18.wireOp",EDGE,"E29.18.0"),sQuery(id+"F18.wireOp",EDGE,"E29.19.0"),sQuery(id+"F18.wireOp",EDGE,"E29.20.0"),sQuery(id+"F18.wireOp",EDGE,"E29.21.0"),sQuery(id+"F18.wireOp",EDGE,"E29.22.0"),sQuery(id+"F18.wireOp",EDGE,"E29.23.0"),sQuery(id+"F18.wireOp",EDGE,"E29.24.0"),sQuery(id+"F18.wireOp",EDGE,"E29.25.0"),sQuery(id+"F18.wireOp",EDGE,"E29.26.0"),sQuery(id+"F18.wireOp",EDGE,"E29.27.0"),sQuery(id+"F18.wireOp",EDGE,"E29.28.0"),sQuery(id+"F18.wireOp",EDGE,"E29.29.0"),sQuery(id+"F18.wireOp",EDGE,"E29.30.0"),sQuery(id+"F18.wireOp",EDGE,"E29.31.0"),sQuery(id+"F18.wireOp",EDGE,"E29.32.0"),sQuery(id+"F18.wireOp",EDGE,"E29.33.0"),sQuery(id+"F18.wireOp",EDGE,"E29.34.0"),sQuery(id+"F18.wireOp",EDGE,"E29.35.0"),sQuery(id+"F18.wireOp",EDGE,"E29.36.0"),sQuery(id+"F18.wireOp",EDGE,"E29.37.0"),sQuery(id+"F18.wireOp",EDGE,"E29.38.0"),sQuery(id+"F18.wireOp",EDGE,"E29.39.0"),sQuery(id+"F18.wireOp",EDGE,"E29.40.0"),sQuery(id+"F18.wireOp",EDGE,"E29.41.0"),sQuery(id+"F18.wireOp",EDGE,"E29.42.0"),sQuery(id+"F18.wireOp",EDGE,"E29.43.0"),sQuery(id+"F18.wireOp",EDGE,"E29.44.0"),sQuery(id+"F18.wireOp",EDGE,"E29.45.0"),sQuery(id+"F18.wireOp",EDGE,"E29.46.0"),sQuery(id+"F18.wireOp",EDGE,"E29.47.0"),sQuery(id+"F18.wireOp",EDGE,"E29.48.0"),sQuery(id+"F18.wireOp",EDGE,"E29.49.0")])],"isStart":false}),makeQuery(id+"F21.opExtrude","CAP_FACE",FACE,{"disambiguationData":[OSD([sQuery(id+"F20.wireOp",EDGE,"E30"),sQuery(id+"F20.wireOp",EDGE,"E32"),sQuery(id+"F20.wireOp",EDGE,"E33"),sQuery(id+"F20.wireOp",EDGE,"E34"),sQuery(id+"F20.wireOp",EDGE,"E35.1.0"),sQuery(id+"F20.wireOp",EDGE,"E35.1.1"),sQuery(id+"F20.wireOp",EDGE,"E35.1.2"),sQuery(id+"F20.wireOp",EDGE,"E35.2.0"),sQuery(id+"F20.wireOp",EDGE,"E35.2.1"),sQuery(id+"F20.wireOp",EDGE,"E35.2.2"),sQuery(id+"F20.wireOp",EDGE,"E35.3.0"),sQuery(id+"F20.wireOp",EDGE,"E35.3.1"),sQuery(id+"F20.wireOp",EDGE,"E35.3.2"),sQuery(id+"F20.wireOp",EDGE,"E35.4.0"),sQuery(id+"F20.wireOp",EDGE,"E35.4.1"),sQuery(id+"F20.wireOp",EDGE,"E35.4.2")])],"isStart":true})]});
            var sketch = newSketch(context, id + "F24", { "sketchPlane" : qUnion([Q0])});
            skCircle(sketch, "E37", {"center": v(-23.99, -14.32) * mm, "radius": 15.88 * mm});
            skSolve(sketch);
        }
        {
            var Q0;
            Q0 = qSketchRegion(id + "F24", true);
            extrude(context, id + "F25", {"entities" : qUnion([Q0]), "operationType" : NewBodyOperationType.ADD, "depth" : 44.45 * mm, "hasSecondDirection" : true, "secondDirectionOppositeDirection" : false, "secondDirectionDepth" : 2.8 * mm});
        }
        {
            var Q0;
            Q0=makeQuery(id+"F15.opExtrude","CAP_FACE",FACE,{"disambiguationData":[OSD([sQuery(id+"F14.wireOp",EDGE,"E18.bottom"),sQuery(id+"F14.wireOp",EDGE,"E18.top"),sQuery(id+"F14.wireOp",EDGE,"E18.left"),sQuery(id+"F14.wireOp",EDGE,"E18.right")])],"isStart":true});
            var sketch = newSketch(context, id + "F26", { "sketchPlane" : qUnion([Q0])});
            skLineSegment(sketch, "E38.bottom", {"start": v(166.83, 161.92) * mm, "end": v(90.63, 161.92) * mm});
            skLineSegment(sketch, "E38.top", {"start": v(166.83, 9.52) * mm, "end": v(90.63, 9.52) * mm});
            skLineSegment(sketch, "E38.left", {"start": v(166.83, 161.92) * mm, "end": v(166.83, 9.52) * mm});
            skLineSegment(sketch, "E38.right", {"start": v(90.63, 161.92) * mm, "end": v(90.63, 9.52) * mm});
            skLineSegment(sketch, "E39.bottom", {"start": v(-137.97, 85.72) * mm, "end": v(-61.77, 85.72) * mm});
            skLineSegment(sketch, "E39.top", {"start": v(-137.97, 161.92) * mm, "end": v(-61.77, 161.92) * mm});
            skLineSegment(sketch, "E39.left", {"start": v(-137.97, 85.72) * mm, "end": v(-137.97, 161.92) * mm});
            skLineSegment(sketch, "E39.right", {"start": v(-61.77, 85.72) * mm, "end": v(-61.77, 161.92) * mm});
            skLineSegment(sketch, "E40.bottom", {"start": v(-137.97, 85.72) * mm, "end": v(-61.15, 85.72) * mm});
            skLineSegment(sketch, "E41.top", {"start": v(-137.97, 9.52) * mm, "end": v(-61.77, 9.52) * mm});
            skLineSegment(sketch, "E41.left", {"start": v(-137.97, 85.72) * mm, "end": v(-137.97, 9.52) * mm});
            skLineSegment(sketch, "E41.right", {"start": v(-61.77, 85.72) * mm, "end": v(-61.77, 9.52) * mm});
            skSolve(sketch);
        }
        {
            var Q0;
            Q0 = qSketchRegion(id + "F26", true);
            extrude(context, id + "F27", {"entities" : qUnion([Q0]), "depth" : 3.17 * mm});
        }
        {
            var Q0;
            Q0=makeQuery(id+"F17.opExtrude","SWEPT_FACE",FACE,{"disambiguationData":[OSD([sQuery(id+"F16.wireOp",EDGE,"E19.bottom")])]});
            var sketch = newSketch(context, id + "F28", { "sketchPlane" : qUnion([Q0])});
            skCircle(sketch, "E42", {"center": v(-15.18, -28.23) * mm, "radius": 7.1 * mm});
            skSolve(sketch);
        }
        {
            var Q0;
            Q0 = qSketchRegion(id + "F28", true);
            extrude(context, id + "F29", {"entities" : qUnion([Q0]), "operationType" : NewBodyOperationType.REMOVE, "oppositeDirection" : true, "depth" : 25.4 * mm});
        }
        {
            var Q0;
            Q0=makeQuery(id+"F9.opExtrude","SWEPT_FACE",FACE,{"disambiguationData":[OSD([sQuery(id+"F8.wireOp",EDGE,"E12.left")])]});
            var sketch = newSketch(context, id + "F30", { "sketchPlane" : qUnion([Q0])});
            skArc(sketch, "E43", {"start": v(53.97, 152.4) * mm, "mid": v(22.22, 184.15) * mm, "end": v(-9.53, 152.4) * mm});
            skArc(sketch, "E44.0", {"start": v(50.8, 152.4) * mm, "mid": v(22.22, 180.97) * mm, "end": v(-6.35, 152.4) * mm});
            skSolve(sketch);
        }
        {
            var Q0;
            Q0 = qSketchRegion(id + "F30", true);
            var Q1;
            {var subQ0=sQuery(id+"F30.wireOp",EDGE,"E43");Q1=makeQuery(id+"F30.imprint","IMPRINT",FACE,{"disambiguationData":[TD([[makeQuery(id+"F30.imprint","IMPRINT",EDGE,{"derivedFrom":subQ0}),1.0]])]});}
            extrude(context, id + "F31", {"entities" : qUnion([Q0, Q1]), "operationType" : NewBodyOperationType.ADD, "oppositeDirection" : true, "depth" : 203.2 * mm});
        }
        {
            var Q0;
            Q0=makeQuery(id+"F9.opExtrude","CAP_FACE",FACE,{"disambiguationData":[OSD([sQuery(id+"F8.wireOp",EDGE,"E12.bottom"),sQuery(id+"F8.wireOp",EDGE,"E12.top"),sQuery(id+"F8.wireOp",EDGE,"E12.left"),sQuery(id+"F8.wireOp",EDGE,"E12.right"),sQuery(id+"F8.wireOp",EDGE,"E13.bottom"),sQuery(id+"F8.wireOp",EDGE,"E13.top"),sQuery(id+"F8.wireOp",EDGE,"E13.left"),sQuery(id+"F8.wireOp",EDGE,"E13.right")])],"isStart":true});
            cPlane(context, id + "F32", {"entities" : qUnion([Q0]), "cplaneType" : CPlaneType.OFFSET, "offset" : 127 * mm, "width" : 152.4 * mm, "height" : 152.4 * mm});
        }
        {
            var Q0;
            Q0=qCreatedBy(id+"F32.planeOp",FACE);
            var sketch = newSketch(context, id + "F33", { "sketchPlane" : qUnion([Q0])});
            skLineSegment(sketch, "E45.MirrorCS", {"start": v(-110.1, 49.82) * mm, "end": v(-109.94, 46.65) * mm});
            skFitSpline(sketch, "E46.MirrorCS", {"points": [v(-110.1, 49.82) * mm, v(-145.03, 20.86) * mm, v(-107.7, -5.7) * mm], "startDerivative": vector(-146.5, -9.13) * mm, "endDerivative": vector(164.8, -2.16) * mm});
            skFitSpline(sketch, "E47.0", {"points": [v(-109.9, 46.65) * mm, v(-115.71, 46.3) * mm, v(-123.05, 44.63) * mm, v(-130.33, 40.9) * mm, v(-134.64, 37.53) * mm, v(-137.9, 33.7) * mm, v(-140.16, 29.54) * mm, v(-141.3, 25.9) * mm, v(-141.75, 22.94) * mm, v(-141.89, 20.71) * mm, v(-141.8, 18.52) * mm, v(-141.42, 15.66) * mm, v(-140.37, 12.24) * mm, v(-138.17, 8.44) * mm, v(-134.9, 5) * mm, v(-130.4, 2.01) * mm, v(-124.47, -0.39) * mm, v(-117.02, -2.03) * mm, v(-110.96, -2.48) * mm, v(-107.65, -2.53) * mm]});
            skLineSegment(sketch, "E48", {"start": v(-107.66, -2.53) * mm, "end": v(-107.7, -5.7) * mm});
            skSolve(sketch);
        }
        {
            var Q0;
            Q0=makeQuery(id+"F33.imprint","IMPRINT",FACE,{"disambiguationData":[TD([[makeQuery(id+"F33.imprint","IMPRINT",EDGE,{"derivedFrom":sQuery(id+"F33.wireOp",EDGE,"E45.MirrorCS")}),-1.0]])]});
            extrude(context, id + "F34", {"entities" : qUnion([Q0]), "operationType" : NewBodyOperationType.ADD, "oppositeDirection" : true, "depth" : 218.44 * mm});
        }
        {
            var Q0;
            Q0=qCreatedBy(id+"F32.planeOp",FACE);
            var sketch = newSketch(context, id + "F35", { "sketchPlane" : qUnion([Q0])});
            skArc(sketch, "E49", {"start": v(117.69, -4.1) * mm, "mid": v(151.45, 23.9) * mm, "end": v(115.96, 49.69) * mm});
            skArc(sketch, "E50.0", {"start": v(118.46, -0.63) * mm, "mid": v(147.9, 23.8) * mm, "end": v(116.95, 46.27) * mm});
            skLineSegment(sketch, "E51", {"start": v(118.46, -0.63) * mm, "end": v(117.69, -4.1) * mm});
            skLineSegment(sketch, "E52", {"start": v(116.95, 46.27) * mm, "end": v(115.96, 49.69) * mm});
            skSolve(sketch);
        }
        {
            var Q0;
            Q0 = qSketchRegion(id + "F35", true);
            extrude(context, id + "F36", {"entities" : qUnion([Q0]), "oppositeDirection" : true, "depth" : 167.13 * mm});
        }
    });
